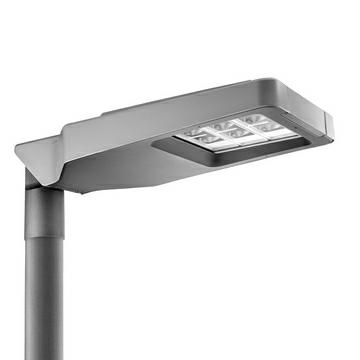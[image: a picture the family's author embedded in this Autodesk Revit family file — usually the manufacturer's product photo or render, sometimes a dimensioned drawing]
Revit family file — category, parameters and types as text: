
# Revit family: Lighting-StreetLighting-GEWISS-ROAD[5]MEDIUM-LED_OPTIC_WIDE_CLII
name_source: partatom
category: Apparecchi per illuminazione
units: mm (PartAtom-declared; Revit-internal decimal feet)

## family parameters
Basato su piano di lavoro = No
Condiviso = No
Punto di calcolo locali = No
Quota connettore circolare = Usa diametro
Sempre verticale = Sì
Sorgente d'illuminazione = No
Taglio con vuoti quando caricato = No
Tipo di parte = Normale

## types (73) — shared parameters
Applicazione = External
Catalogue = LIGHTING
IDF = 569e3ec7-4e66-4966-a072-a472dfe29722
IDT = e2497ca35bdb4cc4a5a8992b37b2b612
IP degree = IP66
Immagine tipo = GWR5276M.jpg
Insulation class = II
Lampada = LED
Produttore = GEWISS S.p.A.
Shock resistance = IK08
Technical sheet = https://www.gewiss.com
URL = https://www.gewiss.com
Version file RFA = 20.11
Warranty = 5 years

## per-type parameters (varying)
- GWR5253M - ROAD5 MEDI WIDE 3M 4000K 0,5A CL2 1-10V: Body=Die-cast aluminium -; Catalogue Range=ROAD [5]; Classification:=-; Color Rendering Index=CRI-70; Colore=Graphite grey; Colour :=Powder coating; Colour temperature=4000K; Colour temperature:=4000 K (CRI>70); Context=Street and parking lighting; Control System=Dimmable 1-10 V; DIN 18032-3 certification=-; Descrizione=GWR5253M - ROAD5 MEDI WIDE 3M 4000K 0,5A CL2 1-10V; Device with reduced surface temperature=-; Driver=Included; Driver Box=Built-in; Efficiency (lm/W)=121; Electrocod=244C; Eletrical and lighting features=-; External screw=Stainless steel; Fixing=Pole Head - Outreach; Gasket=Anti-aging silicone; General information=-; Glow Wire Test :=-; IPEA=ROAD = A5 + // LARGE AREAS = A6 + // CYCLOPEDONALS = A5 + // GREEN AREAS = A5 + // HISTORICAL CENTER = A6 +; Installationa and maintenance=-; LED Life Time (L80B05)=120000H; LED Maintenance=Not available; LED current.=0,5A; Lamp-=LED; Lifetime=L90B10 (Tq+25°C) = 100.000 h - L90B10 (Tq+50°C) = 75.000 h; Locking Hook=Integrated front handle; Lumen output (lm)=7000; Luminaire=LED Road Equipment; Materials=-; Maximum surface exposed to the wind=0,19M2; Maximum surface exposed to the wind :=0.19 m2; Minimum distance from the illuminated object=1M; Modello=GWR5253M; Mouting and installation=Pole Head - Outreach; Nominal flux (lm)=7200; Number of modules=3 (3x3 LED); Operating temperature :=-25 +50 °C; Operating temperature:=-25 +40 °C; Optic=WIDE; Optic :=Metallized polycarbonate reflector; Optic Maintenance=Not available; Optic and illuminating features=-; Overvoltage protection=DM 10KV / CM 10KV; Photobiological Risk Class=RG0; Rated frequency (Hz)=50 / 60; SEO=Street lighting; Shield type=4mm thick flat tempered glass; Standard Deviation Colour Matching=SDCM = 5; Standard-=EN 60598-2-3, EN 60598-1 IEC/TR 62778; Standards and approvals=-; Stocking temperature=-; Supply voltage=220 - 240 V; System power=54W; System power :=58 W @ 0.5A; Tilt adjustable=-20° ÷ +10° side bracket - -10° ÷ +20° pole head; Tilt-=-20° ÷ +10° side bracket - -10° ÷ +20° pole head; Tipologia=Dimmable; Type of light source=LED - Not replaceable; Unified Glare Rating=G*3 - ULOR = 0; Unique digital code (Datamatrix)=Currently not present; Voltage-=220/240 V - 50/60 Hz - Dimmable 1-10 V; Weight (kg):=8; Wiring=Isolating switch
- GWR5213M30K - ROAD5 MEDI WIDE 3M 3000K 1,0A CL2 1-10V: Body=Die-cast aluminium -; Catalogue Range=ROAD [5]; Classification:=-; Color Rendering Index=CRI-70; Colore=Graphite grey; Colour :=Powder coating; Colour temperature=3000K; Colour temperature:=3000 K (CRI>80); Context=Street and parking lighting; Control System=Dimmable 1-10 V; DIN 18032-3 certification=-; Descrizione=GWR5213M30K - ROAD5 MEDI WIDE 3M 3000K 1,0A CL2 1-10V; Device with reduced surface temperature=-; Driver=Included; Driver Box=Built-in; Efficiency (lm/W)=97; Electrocod=244C; Eletrical and lighting features=-; External screw=Stainless steel; Fixing=Pole Head - Outreach; Gasket=Anti-aging silicone; General information=-; Glow Wire Test :=-; IPEA=ROAD = A // LARGE AREAS = A ++ // CYCLOPEDONALS = A // GREEN AREAS = A // HISTORICAL CENTER = A3 +; Installationa and maintenance=-; LED Life Time (L80B05)=120000H; LED Maintenance=Not available; LED current.=1A; Lamp-=LED; Lifetime=L90B10 (Tq+25°C) = 100.000 h - L90B10 (Tq+40°C) = 75.000 h; Locking Hook=Integrated front handle; Lumen output (lm)=11100; Luminaire=LED Road Equipment; Materials=-; Maximum surface exposed to the wind=0,19M2; Maximum surface exposed to the wind :=0.19 m2; Minimum distance from the illuminated object=1M; Modello=GWR5213M30K; Mouting and installation=Pole Head - Outreach; Nominal flux (lm)=12420; Number of modules=3 (3x3 LED); Operating temperature :=-25 +40 °C; Operating temperature:=-25 +40 °C; Optic=WIDE; Optic :=Metallized polycarbonate reflector; Optic Maintenance=Not available; Optic and illuminating features=-; Overvoltage protection=DM 10KV / CM 10KV; Overvoltage resistance :=Common and dfferential mode: 10KV; Photobiological Risk Class=RG0; Power supply operation=Dimmable; Rated frequency (Hz)=50 / 60; SEO=Street lighting; Shield type=4mm thick flat tempered glass; Standard Deviation Colour Matching=SDCM = 5; Standard-=EN 60598-2-3, EN 60598-1 IEC/TR 62778; Standards and approvals=-; Stocking temperature=-; Supply voltage=220 - 240 V; System power=113W; System power :=115 W @ 1A; Tilt adjustable=-20° ÷ +10° side bracket - -10° ÷ +20° pole head; Tilt-=-20° ÷ +10° side bracket - -10° ÷ +20° pole head; Tipo alimentatore=Constant Current Driver Led; Tipologia=Dimmable; Type of light source=LED - Not replaceable; Unified Glare Rating=G*3 - ULOR = 0; Unique digital code (Datamatrix)=Currently not present; Voltage-=220/240 V - 50/60 Hz - Dimmable 1-10 V; Weight (kg):=8; Wiring=Isolating switch
- GWR521630K - ROAD5 MEDI WIDE 6M 3000K 0,85A CL2: Body=Die-cast aluminium -; Catalogue Range=ROAD [5]; Classification:=-; Color Rendering Index=CRI-70; Colore=Graphite grey; Colour :=Powder coating; Colour temperature=3000K; Colour temperature:=3000 K (CRI>80); Context=Street and parking lighting; Control System=Stand alone; DIN 18032-3 certification=-; Descrizione=GWR521630K - ROAD5 MEDI WIDE 6M 3000K 0,85A CL2; Device with reduced surface temperature=-; Driver=Included; Driver Box=Built-in; Efficiency (lm/W)=105; Electrocod=244C; Eletrical and lighting features=-; External screw=Stainless steel; Fixing=Pole Head - Outreach; Gasket=Anti-aging silicone; General information=-; Glow Wire Test :=-; IPEA=ROAD = B // LARGE AREAS = A ++ // CYCLOPEDONALS = A // GREEN AREAS = A // HISTORICAL CENTER = A3 +; Installationa and maintenance=-; LED Life Time (L80B05)=120000H; LED Maintenance=Not available; LED current.=0,849999999999999A; Lamp-=LED; Lifetime=L90B10 (Tq+25°C) = 100.000 h - L90B10 (Tq+40°C) = 50.000 h; Locking Hook=Integrated front handle; Lumen output (lm)=19400; Luminaire=LED Road Equipment; Materials=-; Maximum surface exposed to the wind=0,19M2; Maximum surface exposed to the wind :=0.19 m2; Minimum distance from the illuminated object=1M; Modello=GWR521630K; Mouting and installation=Pole Head - Outreach; Nominal flux (lm)=21114; Number of modules=6 (6x3 LED); Operating temperature :=-25 +40 °C; Operating temperature:=-25 +40 °C; Optic=WIDE; Optic :=Metallized polycarbonate reflector; Optic Maintenance=Not available; Optic and illuminating features=-; Overvoltage protection=DM 10KV / CM 10KV; Overvoltage resistance :=Common and dfferential mode: 10KV; Photobiological Risk Class=RG0; Rated frequency (Hz)=50 / 60; SEO=Street lighting; Shield type=4mm thick flat tempered glass; Standard Deviation Colour Matching=SDCM = 5; Standard-=EN 60598-2-3, EN 60598-1 IEC/TR 62778; Standards and approvals=-; Stocking temperature=-; Supply voltage=220 - 240 V; System power=185W; System power :=185 W @ 0.85A; Tilt adjustable=-20° ÷ +10° side bracket - -10° ÷ +20° pole head; Tilt-=-20° ÷ +10° side bracket - -10° ÷ +20° pole head; Tipo alimentatore=Constant Current Driver Led; Tipologia=Stand alone; Type of light source=LED - Not replaceable; Unified Glare Rating=G*3 - ULOR = 0; Unique digital code (Datamatrix)=Currently not present; Voltage-=220/240 V - 50/60 Hz - Stand alone; Weight (kg):=9,09999999999999; Wiring=Isolating switch
- GWR5254B - ROAD5 MEDI WIDE 4M 4000K 0,5A CL2 BIREG: Body=Die-cast aluminium -; Catalogue Range=ROAD [5]; Classification:=-; Color Rendering Index=CRI-70; Colore=Graphite grey; Colour :=Powder coating; Colour temperature=4000K; Colour temperature:=4000 K (CRI>70); Context=Street and parking lighting; Control System=Bi-power with self-learning; DIN 18032-3 certification=-; Descrizione=GWR5254B - ROAD5 MEDI WIDE 4M 4000K 0,5A CL2 BIREG; Device with reduced surface temperature=-; Driver=Included; Driver Box=Built-in; Efficiency (lm/W)=124; Electrocod=244C; Eletrical and lighting features=-; External screw=Stainless steel; Fixing=Pole Head - Outreach; Gasket=Anti-aging silicone; General information=-; Glow Wire Test :=-; IPEA=ROAD = A5 + // LARGE AREAS = A6 + // CYCLOPEDONALS = A4 + // GREEN AREAS = A4 + // HISTORICAL CENTER = A6 +; Installationa and maintenance=-; LED Life Time (L80B05)=120000H; LED Maintenance=Not available; LED current.=0,5A; Lamp-=LED; Lifetime=L90B10 (Tq+25°C) = 100.000 h - L90B10 (Tq+50°C) = 50.000 h; Locking Hook=Integrated front handle; Lumen output (lm)=9400; Luminaire=LED Road Equipment; Materials=-; Maximum surface exposed to the wind=0,19M2; Maximum surface exposed to the wind :=0.19 m2; Minimum distance from the illuminated object=1M; Modello=GWR5254B; Mouting and installation=Pole Head - Outreach; Nominal flux (lm)=9600; Number of modules=4 (4x3 LED); Operating temperature :=-25 +50 °C; Operating temperature:=-25 +40 °C; Optic=WIDE; Optic :=Metallized polycarbonate reflector; Optic Maintenance=Not available; Optic and illuminating features=-; Overvoltage protection=DM 10KV / CM 10KV; Photobiological Risk Class=RG0; Power supply operation=Bi power; Rated frequency (Hz)=50 / 60; SEO=Street lighting; Shield type=4mm thick flat tempered glass; Standard Deviation Colour Matching=SDCM = 5; Standard-=EN 60598-2-3, EN 60598-1 IEC/TR 62778; Standards and approvals=-; Stocking temperature=-; Supply voltage=220 - 240 V; System power=73W; System power :=76 W @ 0.5A; Tilt adjustable=-20° ÷ +10° side bracket - -10° ÷ +20° pole head; Tilt-=-20° ÷ +10° side bracket - -10° ÷ +20° pole head; Type of light source=LED - Not replaceable; Unified Glare Rating=G*3 - ULOR = 0; Unique digital code (Datamatrix)=Currently not present; Voltage-=220/240 V - 50/60 Hz - Bi-power with self-learning; Weight (kg):=8,4; Wiring=Isolating switch
- GWR5216M30K - ROAD5 MEDI WIDE 6M 3000K 0,85A CL2 1-10V: Body=Die-cast aluminium -; Catalogue Range=ROAD [5]; Classification:=-; Color Rendering Index=CRI-70; Colore=Graphite grey; Colour :=Powder coating; Colour temperature=3000K; Colour temperature:=3000 K (CRI>80); Context=Street and parking lighting; Control System=Dimmable 1-10 V; DIN 18032-3 certification=-; Descrizione=GWR5216M30K - ROAD5 MEDI WIDE 6M 3000K 0,85A CL2 1-10V; Device with reduced surface temperature=-; Driver=Included; Driver Box=Built-in; Efficiency (lm/W)=104; Electrocod=244C; Eletrical and lighting features=-; External screw=Stainless steel; Fixing=Pole Head - Outreach; Gasket=Anti-aging silicone; General information=-; Glow Wire Test :=-; IPEA=ROAD = B // LARGE AREAS = A ++ // CYCLOPEDONALS = A // GREEN AREAS = A // HISTORICAL CENTER = A3 +; Installationa and maintenance=-; LED Life Time (L80B05)=120000H; LED Maintenance=Not available; LED current.=0,849999999999999A; Lamp-=LED; Lifetime=L90B10 (Tq+25°C) = 100.000 h - L90B10 (Tq+40°C) = 50.000 h; Locking Hook=Integrated front handle; Lumen output (lm)=19400; Luminaire=LED Road Equipment; Materials=-; Maximum surface exposed to the wind=0,19M2; Maximum surface exposed to the wind :=0.19 m2; Minimum distance from the illuminated object=1M; Modello=GWR5216M30K; Mouting and installation=Pole Head - Outreach; Nominal flux (lm)=21114; Number of modules=6 (6x3 LED); Operating temperature :=-25 +40 °C; Operating temperature:=-25 +40 °C; Optic=WIDE; Optic :=Metallized polycarbonate reflector; Optic Maintenance=Not available; Optic and illuminating features=-; Overvoltage protection=DM 10KV / CM 10KV; Overvoltage resistance :=Common and dfferential mode: 10KV; Photobiological Risk Class=RG0; Power supply operation=Dimmable; Rated frequency (Hz)=50 / 60; SEO=Street lighting; Shield type=4mm thick flat tempered glass; Standard Deviation Colour Matching=SDCM = 5; Standard-=EN 60598-2-3, EN 60598-1 IEC/TR 62778; Standards and approvals=-; Stocking temperature=-; Supply voltage=220 - 240 V; System power=185W; System power :=187 W @ 0.85A; Tilt adjustable=-20° ÷ +10° side bracket - -10° ÷ +20° pole head; Tilt-=-20° ÷ +10° side bracket - -10° ÷ +20° pole head; Tipo alimentatore=Constant Current Driver Led; Tipologia=Dimmable; Type of light source=LED - Not replaceable; Unified Glare Rating=G*3 - ULOR = 0; Unique digital code (Datamatrix)=Currently not present; Voltage-=220/240 V - 50/60 Hz - Dimmable 1-10 V; Weight (kg):=9,09999999999999; Wiring=Isolating switch
- GWR5256D30K - ROAD5 MEDI WIDE 6M 3000K 0,5A CL2: Body=Die-cast aluminium -; Classification:=-; Color Rendering Index=CRI-70; Colore=Graphite grey; Colour :=Powder coating; Colour temperature=3000K; Context=Street and parking lighting; Control System=DALI; DIN 18032-3 certification=-; Descrizione=GWR5256D30K - ROAD5 MEDI WIDE 6M 3000K 0,5A CL2; Device with reduced surface temperature=-; Driver=Included; Driver Box=Built-in; Efficiency (lm/W)=108; Eletrical and lighting features=-; External screw=Stainless steel; Fixing=Pole Head - Outreach; Gasket=Anti-aging silicone; General information=-; Glow Wire Test :=-; IPEA=ROAD = A ++ // LARGE AREAS = A4 + // CYCLOPEDONALS = A + // GREEN AREAS = A + // HISTORICAL CENTER = A5 +; Installationa and maintenance=-; LED Maintenance=Not available; Lifetime=L90B10 (Tq+25°C) = 100.000 h - L90B10 (Tq+50°C) = 50.000 h; Locking Hook=Integrated front handle; Lumen output (lm)=12200; Luminaire=LED Road Equipment; Materials=-; Maximum surface exposed to the wind :=0.19 m2; Modello=GWR5256D30K; Mouting and installation=Pole Head - Outreach; Number of modules=6 (6x3 LED); Operating temperature :=-25 +50 °C; Optic=WIDE; Optic :=Metallized polycarbonate reflector; Optic Maintenance=Not available; Optic and illuminating features=-; Overvoltage protection=DM 10KV / CM 10KV; Photobiological Risk Class=RG0; Rated frequency (Hz)=50 / 60; SEO=Street lighting; Shield type=4mm thick flat tempered glass; Standard Deviation Colour Matching=SDCM = 5; Standard-=EN 60598-2-3, EN 60598-1 IEC/TR 62778; Standards and approvals=-; Stocking temperature=-; Supply voltage=220 - 240 V; System power :=113 W @ 0.5A; Tilt-=-20° ÷ +10° side bracket - -10° ÷ +20° pole head; Type of light source=LED - Not replaceable; Unified Glare Rating=G*3 - ULOR = 0; Unique digital code (Datamatrix)=Currently not present; Weight (kg):=9,09999999999999; Wiring=Isolating switch
- GWR5253B - ROAD5 MEDI WIDE 3M 4000K 0,5A CL2 BIREG: Body=Die-cast aluminium -; Catalogue Range=ROAD [5]; Classification:=-; Color Rendering Index=CRI-70; Colore=Graphite grey; Colour :=Powder coating; Colour temperature=4000K; Colour temperature:=4000 K (CRI>70); Context=Street and parking lighting; Control System=Bi-power with self-learning; DIN 18032-3 certification=-; Descrizione=GWR5253B - ROAD5 MEDI WIDE 3M 4000K 0,5A CL2 BIREG; Device with reduced surface temperature=-; Driver=Included; Driver Box=Built-in; Efficiency (lm/W)=121; Electrocod=244C; Eletrical and lighting features=-; External screw=Stainless steel; Fixing=Pole Head - Outreach; Gasket=Anti-aging silicone; General information=-; Glow Wire Test :=-; IPEA=ROAD = A5 + // LARGE AREAS = A6 + // CYCLOPEDONALS = A5 + // GREEN AREAS = A5 + // HISTORICAL CENTER = A6 +; Installationa and maintenance=-; LED Life Time (L80B05)=120000H; LED Maintenance=Not available; LED current.=0,5A; Lamp-=LED; Lifetime=L90B10 (Tq+25°C) = 100.000 h - L90B10 (Tq+50°C) = 75.000 h; Locking Hook=Integrated front handle; Lumen output (lm)=7000; Luminaire=LED Road Equipment; Materials=-; Maximum surface exposed to the wind=0,19M2; Maximum surface exposed to the wind :=0.19 m2; Minimum distance from the illuminated object=1M; Modello=GWR5253B; Mouting and installation=Pole Head - Outreach; Nominal flux (lm)=7200; Number of modules=3 (3x3 LED); Operating temperature :=-25 +50 °C; Operating temperature:=-25 +40 °C; Optic=WIDE; Optic :=Metallized polycarbonate reflector; Optic Maintenance=Not available; Optic and illuminating features=-; Overvoltage protection=DM 10KV / CM 10KV; Photobiological Risk Class=RG0; Power supply operation=Bi power; Rated frequency (Hz)=50 / 60; SEO=Street lighting; Shield type=4mm thick flat tempered glass; Standard Deviation Colour Matching=SDCM = 5; Standard-=EN 60598-2-3, EN 60598-1 IEC/TR 62778; Standards and approvals=-; Stocking temperature=-; Supply voltage=220 - 240 V; System power=54W; System power :=58 W @ 0.5A; Tilt adjustable=-20° ÷ +10° side bracket - -10° ÷ +20° pole head; Tilt-=-20° ÷ +10° side bracket - -10° ÷ +20° pole head; Type of light source=LED - Not replaceable; Unified Glare Rating=G*3 - ULOR = 0; Unique digital code (Datamatrix)=Currently not present; Voltage-=220/240 V - 50/60 Hz - Bi-power with self-learning; Weight (kg):=8; Wiring=Isolating switch
- GWR5215M30K - ROAD5 MEDI WIDE 5M 3000K 0,85A CL2 1-10V: Body=Die-cast aluminium -; Catalogue Range=ROAD [5]; Classification:=-; Color Rendering Index=CRI-70; Colore=Graphite grey; Colour :=Powder coating; Colour temperature=3000K; Colour temperature:=3000 K (CRI>80); Context=Street and parking lighting; Control System=Dimmable 1-10 V; DIN 18032-3 certification=-; Descrizione=GWR5215M30K - ROAD5 MEDI WIDE 5M 3000K 0,85A CL2 1-10V; Device with reduced surface temperature=-; Driver=Included; Driver Box=Built-in; Efficiency (lm/W)=101; Electrocod=244C; Eletrical and lighting features=-; External screw=Stainless steel; Fixing=Pole Head - Outreach; Gasket=Anti-aging silicone; General information=-; Glow Wire Test :=-; IPEA=ROAD = A // LARGE AREAS = A ++ // CYCLOPEDONALS = A // GREEN AREAS = A // HISTORICAL CENTER = A4 +; Installationa and maintenance=-; LED Life Time (L80B05)=120000H; LED Maintenance=Not available; LED current.=0,849999999999999A; Lamp-=LED; Lifetime=L90B10 (Tq+25°C) = 100.000 h - L90B10 (Tq+40°C) = 50.000 h; Locking Hook=Integrated front handle; Lumen output (lm)=16200; Luminaire=LED Road Equipment; Materials=-; Maximum surface exposed to the wind=0,19M2; Maximum surface exposed to the wind :=0.19 m2; Minimum distance from the illuminated object=1M; Modello=GWR5215M30K; Mouting and installation=Pole Head - Outreach; Nominal flux (lm)=18423; Number of modules=5 (5x3 LED); Operating temperature :=-25 +40 °C; Operating temperature:=-25 +40 °C; Optic=WIDE; Optic :=Metallized polycarbonate reflector; Optic Maintenance=Not available; Optic and illuminating features=-; Overvoltage protection=DM 10KV / CM 10KV; Overvoltage resistance :=Common and dfferential mode: 10KV; Photobiological Risk Class=RG0; Power supply operation=Dimmable; Rated frequency (Hz)=50 / 60; SEO=Street lighting; Shield type=4mm thick flat tempered glass; Standard Deviation Colour Matching=SDCM = 5; Standard-=EN 60598-2-3, EN 60598-1 IEC/TR 62778; Standards and approvals=-; Stocking temperature=-; Supply voltage=220 - 240 V; System power=159W; System power :=161 W @ 0.85A; Tilt adjustable=-20° ÷ +10° side bracket - -10° ÷ +20° pole head; Tilt-=-20° ÷ +10° side bracket - -10° ÷ +20° pole head; Tipo alimentatore=Constant Current Driver Led; Tipologia=Dimmable; Type of light source=LED - Not replaceable; Unified Glare Rating=G*3 - ULOR = 0; Unique digital code (Datamatrix)=Currently not present; Voltage-=220/240 V - 50/60 Hz - Dimmable 1-10 V; Weight (kg):=8,8; Wiring=Isolating switch
- GWR5274B - ROAD5 MEDI WIDE 4M 4000K 0,7A CL2 BIREG: Catalogue Range=ROAD [5]; Colour temperature=4000 K (CRI 70); Colour temperature:=4000 K (CRI 70); Descrizione=ROAD 5 MED.BIPOW.4M 4000K 700mA OPT.W; EAN code=8011564858466; Electrocod=244C; LED LifeTime (L80B05)=77000H; LED current.=0,7A; Lamp-=LED; Lumen output (lm)=10480; Maximum surface exposed to the wind=0,19M2; Minimum distance from the illuminated object=1M; Modello=GWR5274B; No. Chorus modules=4 (4x3 LED); Nominal flux (lm)=12480; Number of modules=4 (4x3 LED); Operating temperature:=-25 +50 °C; Optic=W - ULOR: 0%; Overvoltage resistance=12 KV (Common and dfferential mode); Pilot current=0,7A; Power supply operation=Bi power; SEO=Street lighting; System power=108W; Tilt adjustable=-20° ÷ +10° side bracket - -10° ÷ +20° pole head; Tipo alimentatore=Constant Current Driver Led; Tipologia=Bi power; Voltage-=220/240 V - 50/60 Hz - Bi-power with self-learning; Weight (kg):=8,4; Working temperature=-25 +50 °C
- GWR5213M - ROAD 5 MED.DIMM.3M 4000K 1A OPT.W: Catalogue Range=ROAD [5]; Colour temperature=4000 K (CRI 70); Colour temperature:=4000 K (CRI 70); Descrizione=ROAD 5 MED.DIMM.3M 4000K 1A OPT.W; EAN code=8011564858640; Electrocod=244C; LED LifeTime (L80B05)=120000H; LED current.=1A; Lamp-=LED; Lumen output (lm)=11520; Maximum surface exposed to the wind=0,19M2; Minimum distance from the illuminated object=1M; Modello=GWR5213M; No. Chorus modules=3 (3x3 LED); Nominal flux (lm)=14310; Number of modules=3 (3x3 LED); Operating temperature:=-25 +40 °C; Optic=W - ULOR: 0%; Overvoltage resistance=12 KV (Common and dfferential mode); Pilot current=1A; Power supply operation=Dimmable; SEO=Street lighting; System power=113W; Tilt adjustable=-20° ÷ +10° side bracket - -10° ÷ +20° pole head; Tipo alimentatore=Constant Current Driver Led; Tipologia=Dimmable; Voltage-=220/240 V - 50/60 Hz - Dimmable 1-10 V; Weight (kg)=8; Weight (kg):=8; Working temperature=-25 +40 °C
- GWR527430K - ROAD5 MEDI WIDE 4M 3000K 0,7A CL2: Body=Die-cast aluminium -; Catalogue Range=ROAD [5]; Classification:=-; Color Rendering Index=CRI-70; Colore=Graphite grey; Colour :=Powder coating; Colour temperature=3000K; Colour temperature:=3000 K (CRI>80); Context=Street and parking lighting; Control System=Stand alone; DIN 18032-3 certification=-; Descrizione=GWR527430K - ROAD5 MEDI WIDE 4M 3000K 0,7A CL2; Device with reduced surface temperature=-; Driver=Included; Driver Box=Built-in; Efficiency (lm/W)=104; Electrocod=244C; Eletrical and lighting features=-; External screw=Stainless steel; Fixing=Pole Head - Outreach; Gasket=Anti-aging silicone; General information=-; Glow Wire Test :=-; IPEA=ROAD = A + // LARGE AREAS = A3 + // CYCLOPEDONALS = A + // GREEN AREAS = A + // HISTORICAL CENTER = A4 +; Installationa and maintenance=-; LED Life Time (L80B05)=77000H; LED Maintenance=Not available; LED current.=0,7A; Lamp-=LED; Lifetime=L90B10 (Tq+25°C) = 100.000 h - L90B10 (Tq+50°C) = 50.000 h; Locking Hook=Integrated front handle; Lumen output (lm)=11000; Luminaire=LED Road Equipment; Materials=-; Maximum surface exposed to the wind=0,19M2; Maximum surface exposed to the wind :=0.19 m2; Minimum distance from the illuminated object=1M; Modello=GWR527430K; Mouting and installation=Pole Head - Outreach; Nominal flux (lm)=10800; Number of modules=4 (4x3 LED); Operating temperature :=-25 +50 °C; Operating temperature:=-25 +50 °C; Optic=WIDE; Optic :=Metallized polycarbonate reflector; Optic Maintenance=Not available; Optic and illuminating features=-; Overvoltage protection=DM 10KV / CM 10KV; Overvoltage resistance :=Common and dfferential mode: 10KV; Photobiological Risk Class=RG0; Rated frequency (Hz)=50 / 60; SEO=Street lighting; Shield type=4mm thick flat tempered glass; Standard Deviation Colour Matching=SDCM = 5; Standard-=EN 60598-2-3, EN 60598-1 IEC/TR 62778; Standards and approvals=-; Stocking temperature=-; Supply voltage=220 - 240 V; System power=106W; System power :=106 W @ 0.7A; Tilt adjustable=-20° ÷ +10° side bracket - -10° ÷ +20° pole head; Tilt-=-20° ÷ +10° side bracket - -10° ÷ +20° pole head; Tipo alimentatore=Constant Current Driver Led; Tipologia=Stand alone; Type of light source=LED - Not replaceable; Unified Glare Rating=G*3 - ULOR = 0; Unique digital code (Datamatrix)=Currently not present; Voltage-=220/240 V - 50/60 Hz - Stand alone; Weight (kg):=8,4; Wiring=Isolating switch
- GWR5275B - ROAD5 MEDI WIDE 5M 4000K 0,7A CL2 BIREG: Catalogue Range=ROAD [5]; Colour temperature=4000 K (CRI 70); Colour temperature:=4000 K (CRI 70); Descrizione=ROAD 5 MED.BIPOW.5M 4000K 700mA OPT.W; EAN code=8011564858497; Electrocod=244C; LED LifeTime (L80B05)=77000H; LED current.=0,7A; Lamp-=LED; Lumen output (lm)=13100; Maximum surface exposed to the wind=0,19M2; Minimum distance from the illuminated object=1M; Modello=GWR5275B; No. Chorus modules=5 (5x3 LED); Nominal flux (lm)=15600; Number of modules=5 (5x3 LED); Operating temperature:=-25 +50 °C; Optic=W - ULOR: 0%; Overvoltage resistance=12 KV (Common and dfferential mode); Pilot current=0,7A; Power supply operation=Bi power; SEO=Street lighting; System power=134W; Tilt adjustable=-20° ÷ +10° side bracket - -10° ÷ +20° pole head; Tipo alimentatore=Constant Current Driver Led; Tipologia=Bi power; Voltage-=220/240 V - 50/60 Hz - Bi-power with self-learning; Weight (kg)=8,8; Weight (kg):=8,8; Working temperature=-25 +50 °C
- GWR5275 - ROAD 5 MED.ST.AL.5M 4000K 700mA OPT.W: Catalogue Range=ROAD [5]; Colour temperature=4000 K (CRI 70); Colour temperature:=4000 K (CRI 70); Descrizione=ROAD 5 MED.ST.AL.5M 4000K 700mA OPT.W; EAN code=8011564858305; Electrocod=244C; LED LifeTime (L80B05)=77000H; LED current.=0,7A; Lamp-=LED; Lumen output (lm)=13100; Maximum surface exposed to the wind=0,19M2; Minimum distance from the illuminated object=1M; Modello=GWR5275; No. Chorus modules=5 (5x3 LED); Nominal flux (lm)=15600; Number of modules=5 (5x3 LED); Operating temperature:=-25 +50 °C; Optic=W - ULOR: 0%; Overvoltage resistance=12 KV (Common and dfferential mode); Pilot current=0,7A; SEO=Street lighting; System power=132W; Tilt adjustable=-20° ÷ +10° side bracket - -10° ÷ +20° pole head; Tipo alimentatore=Constant Current Driver Led; Tipologia=Stand alone; Voltage-=220/240 V - 50/60 Hz - Stand alone; Weight (kg)=8,8; Weight (kg):=8,8; Working temperature=-25 +50 °C
- GWR5276M30K - ROAD5 MEDI WIDE 6M 3000K 0,7A CL2 1-10V: Body=Die-cast aluminium -; Catalogue Range=ROAD [5]; Classification:=-; Color Rendering Index=CRI-70; Colore=Graphite grey; Colour :=Powder coating; Colour temperature=3000K; Colour temperature:=3000 K (CRI>80); Context=Street and parking lighting; Control System=Dimmable 1-10 V; DIN 18032-3 certification=-; Descrizione=GWR5276M30K - ROAD5 MEDI WIDE 6M 3000K 0,7A CL2 1-10V; Device with reduced surface temperature=-; Driver=Included; Driver Box=Built-in; Efficiency (lm/W)=102; Electrocod=244C; Eletrical and lighting features=-; External screw=Stainless steel; Fixing=Pole Head - Outreach; Gasket=Anti-aging silicone; General information=-; Glow Wire Test :=-; IPEA=ROAD = A // LARGE AREAS = A3 + // CYCLOPEDONALS = A // GREEN AREAS = A // HISTORICAL CENTER = A4 +; Installationa and maintenance=-; LED Life Time (L80B05)=77000H; LED Maintenance=Not available; LED current.=0,7A; Lamp-=LED; Lifetime=L90B10 (Tq+25°C) = 100.000 h - L90B10 (Tq+50°C) = 50.000 h; Locking Hook=Integrated front handle; Lumen output (lm)=16500; Luminaire=LED Road Equipment; Materials=-; Maximum surface exposed to the wind=0,19M2; Maximum surface exposed to the wind :=0.19 m2; Minimum distance from the illuminated object=1M; Modello=GWR5276M30K; Mouting and installation=Pole Head - Outreach; Nominal flux (lm)=16200; Number of modules=6 (6x3 LED); Operating temperature :=-25 +50 °C; Operating temperature:=-25 +50 °C; Optic=WIDE; Optic :=Metallized polycarbonate reflector; Optic Maintenance=Not available; Optic and illuminating features=-; Overvoltage protection=DM 10KV / CM 10KV; Overvoltage resistance :=Common and dfferential mode: 10KV; Photobiological Risk Class=RG0; Power supply operation=Dimmable; Rated frequency (Hz)=50 / 60; SEO=Street lighting; Shield type=4mm thick flat tempered glass; Standard Deviation Colour Matching=SDCM = 5; Standard-=EN 60598-2-3, EN 60598-1 IEC/TR 62778; Standards and approvals=-; Stocking temperature=-; Supply voltage=220 - 240 V; System power=159W; System power :=161 W @ 0.7A; Tilt adjustable=-20° ÷ +10° side bracket - -10° ÷ +20° pole head; Tilt-=-20° ÷ +10° side bracket - -10° ÷ +20° pole head; Tipo alimentatore=Constant Current Driver Led; Tipologia=Dimmable; Type of light source=LED - Not replaceable; Unified Glare Rating=G*3 - ULOR = 0; Unique digital code (Datamatrix)=Currently not present; Voltage-=220/240 V - 50/60 Hz - Dimmable 1-10 V; Weight (kg):=9,09999999999999; Wiring=Isolating switch
- GWR5274B30K - ROAD5 MEDI WIDE 4M 3000K 0,7A CL2 BIREG: Body=Die-cast aluminium -; Catalogue Range=ROAD [5]; Classification:=-; Color Rendering Index=CRI-70; Colore=Graphite grey; Colour :=Powder coating; Colour temperature=3000K; Colour temperature:=3000 K (CRI>80); Context=Street and parking lighting; Control System=Bi-power with self-learning; DIN 18032-3 certification=-; Descrizione=GWR5274B30K - ROAD5 MEDI WIDE 4M 3000K 0,7A CL2 BIREG; Device with reduced surface temperature=-; Driver=Included; Driver Box=Built-in; Efficiency (lm/W)=102; Electrocod=244C; Eletrical and lighting features=-; External screw=Stainless steel; Fixing=Pole Head - Outreach; Gasket=Anti-aging silicone; General information=-; Glow Wire Test :=-; IPEA=ROAD = A + // LARGE AREAS = A3 + // CYCLOPEDONALS = A // GREEN AREAS = A // HISTORICAL CENTER = A4 +; Installationa and maintenance=-; LED Life Time (L80B05)=77000H; LED Maintenance=Not available; LED current.=0,7A; Lamp-=LED; Lifetime=L90B10 (Tq+25°C) = 100.000 h - L90B10 (Tq+50°C) = 50.000 h; Locking Hook=Integrated front handle; Lumen output (lm)=11000; Luminaire=LED Road Equipment; Materials=-; Maximum surface exposed to the wind=0,19M2; Maximum surface exposed to the wind :=0.19 m2; Minimum distance from the illuminated object=1M; Modello=GWR5274B30K; Mouting and installation=Pole Head - Outreach; Nominal flux (lm)=10800; Number of modules=4 (4x3 LED); Operating temperature :=-25 +50 °C; Operating temperature:=-25 +50 °C; Optic=WIDE; Optic :=Metallized polycarbonate reflector; Optic Maintenance=Not available; Optic and illuminating features=-; Overvoltage protection=DM 10KV / CM 10KV; Overvoltage resistance :=Common and dfferential mode: 10KV; Photobiological Risk Class=RG0; Power supply operation=Bi power; Rated frequency (Hz)=50 / 60; SEO=Street lighting; Shield type=4mm thick flat tempered glass; Standard Deviation Colour Matching=SDCM = 5; Standard-=EN 60598-2-3, EN 60598-1 IEC/TR 62778; Standards and approvals=-; Stocking temperature=-; Supply voltage=220 - 240 V; System power=108W; System power :=108 W @ 0.7A; Tilt adjustable=-20° ÷ +10° side bracket - -10° ÷ +20° pole head; Tilt-=-20° ÷ +10° side bracket - -10° ÷ +20° pole head; Tipo alimentatore=Constant Current Driver Led; Tipologia=Bi power; Type of light source=LED - Not replaceable; Unified Glare Rating=G*3 - ULOR = 0; Unique digital code (Datamatrix)=Currently not present; Voltage-=220/240 V - 50/60 Hz - Bi-power with self-learning; Weight (kg):=8,4; Wiring=Isolating switch
- GWR5216 - ROAD 5 MED.ST.AL.6M 4000K 0,85A OPT.W: Catalogue Range=ROAD [5]; Colour temperature=4000 K (CRI 70); Colour temperature:=4000 K (CRI 70); Descrizione=ROAD 5 MED.ST.AL.6M 4000K 0,85A OPT.W; EAN code=8011564858435; Electrocod=244C; LED LifeTime (L80B05)=120000H; LED current.=0,85A; Lamp-=LED; Lumen output (lm)=19580; Maximum surface exposed to the wind=0,19M2; Minimum distance from the illuminated object=1M; Modello=GWR5216; No. Chorus modules=6 (6x3 LED); Nominal flux (lm)=24330; Number of modules=6 (6x3 LED); Operating temperature:=-25 +40 °C; Optic=W - ULOR: 0%; Overvoltage resistance=12 KV (Common and dfferential mode); Pilot current=0,85A; SEO=Street lighting; System power=185W; Tilt adjustable=-20° ÷ +10° side bracket - -10° ÷ +20° pole head; Tipo alimentatore=Constant Current Driver Led; Tipologia=Stand alone; Voltage-=220/240 V - 50/60 Hz - Stand alone; Weight (kg)=9.1; Weight (kg):=9,1; Working temperature=-25 +40 °C
- GWR5275V - ROAD5 MEDI V.WIDE 5M 4000K 0,7A CL2: Body=Die-cast aluminium -; Catalogue Range=ROAD [5]; Classification:=-; Color Rendering Index=CRI-70; Colore=Graphite grey; Colour :=Powder coating; Colour temperature=4000K; Colour temperature:=4000 K (CRI>70); Context=Street and parking lighting; Control System=DALI - 5 Step; DIN 18032-3 certification=-; Descrizione=GWR5275V - ROAD5 MEDI V.WIDE 5M 4000K 0,7A CL2; Device with reduced surface temperature=-; Driver=Included; Driver Box=Built-in; Efficiency (lm/W)=118; Electrocod=244C; Eletrical and lighting features=-; External screw=Stainless steel; Fixing=Pole Head - Outreach; Gasket=Anti-aging silicone; General information=-; Glow Wire Test :=-; IPEA=ROAD = A ++ // LARGE AREAS = A5 + // CYCLOPEDONALS = A ++ // GREEN AREAS = A ++ // HISTORICAL CENTER = A6 +; Installationa and maintenance=-; LED Life Time (L80B05)=120000H; LED Maintenance=Not available; LED current.=0,7A; Lamp-=LED; Lifetime=L90B10 (Tq+25°C) = 100.000 h - L90B10 (Tq+50°C) = 50.000 h; Locking Hook=Integrated front handle; Lumen output (lm)=15800; Luminaire=LED Road Equipment; Materials=-; Maximum surface exposed to the wind=0,19M2; Maximum surface exposed to the wind :=0.19 m2; Minimum distance from the illuminated object=1M; Modello=GWR5275V; Mouting and installation=Pole Head - Outreach; Nominal flux (lm)=15600; Number of modules=5 (5x3 LED); Operating temperature :=-25 +50 °C; Operating temperature:=-25 +40 °C; Optic=WIDE; Optic :=Metallized polycarbonate reflector; Optic Maintenance=Not available; Optic and illuminating features=-; Overvoltage protection=DM 10KV / CM 10KV; Photobiological Risk Class=RG0; Rated frequency (Hz)=50 / 60; SEO=Street lighting; Shield type=4mm thick flat tempered glass; Standard Deviation Colour Matching=SDCM = 5; Standard-=EN 60598-2-3, EN 60598-1 IEC/TR 62778; Standards and approvals=-; Stocking temperature=-; Supply voltage=220 - 240 V; System power=132W; System power :=134 W @ 0.7A; Tilt adjustable=-20° ÷ +10° side bracket - -10° ÷ +20° pole head; Tilt-=-20° ÷ +10° side bracket - -10° ÷ +20° pole head; Tipologia=Programmable (5 step); Type of light source=LED - Not replaceable; Unified Glare Rating=G*3 - ULOR = 0; Unique digital code (Datamatrix)=Currently not present; Voltage-=220/240 V - 50/60 Hz - Stand alone and/or programmable; Weight (kg):=8,8; Wiring=Isolating switch
- GWR5273V - ROAD5 MEDI V.WIDE 3M 4000K 0,7A CL2: Body=Die-cast aluminium -; Catalogue Range=ROAD [5]; Classification:=-; Color Rendering Index=CRI-70; Colore=Graphite grey; Colour :=Powder coating; Colour temperature=4000K; Colour temperature:=4000 K (CRI>70); Context=Street and parking lighting; Control System=DALI - 5 Step; DIN 18032-3 certification=-; Descrizione=GWR5273V - ROAD5 MEDI V.WIDE 3M 4000K 0,7A CL2; Device with reduced surface temperature=-; Driver=Included; Driver Box=Built-in; Efficiency (lm/W)=117; Electrocod=244C; Eletrical and lighting features=-; External screw=Stainless steel; Fixing=Pole Head - Outreach; Gasket=Anti-aging silicone; General information=-; Glow Wire Test :=-; IPEA=ROAD = A4 + // LARGE AREAS = A5 + // CYCLOPEDONALS = A3 + // GREEN AREAS = A3 + // HISTORICAL CENTER = A6 +; Installationa and maintenance=-; LED Life Time (L80B05)=120000H; LED Maintenance=Not available; LED current.=0,7A; Lamp-=LED; Lifetime=L90B10 (Tq+25°C) = 100.000 h - L90B10 (Tq+50°C) = 75.000 h; Locking Hook=Integrated front handle; Lumen output (lm)=9500; Luminaire=LED Road Equipment; Materials=-; Maximum surface exposed to the wind=0,19M2; Maximum surface exposed to the wind :=0.19 m2; Minimum distance from the illuminated object=1M; Modello=GWR5273V; Mouting and installation=Pole Head - Outreach; Nominal flux (lm)=9360; Number of modules=3 (3x3 LED); Operating temperature :=-25 +50 °C; Operating temperature:=-25 +40 °C; Optic=WIDE; Optic :=Metallized polycarbonate reflector; Optic Maintenance=Not available; Optic and illuminating features=-; Overvoltage protection=DM 10KV / CM 10KV; Photobiological Risk Class=RG0; Rated frequency (Hz)=50 / 60; SEO=Street lighting; Shield type=4mm thick flat tempered glass; Standard Deviation Colour Matching=SDCM = 5; Standard-=EN 60598-2-3, EN 60598-1 IEC/TR 62778; Standards and approvals=-; Stocking temperature=-; Supply voltage=220 - 240 V; System power=79W; System power :=81 W @ 0.7A; Tilt adjustable=-20° ÷ +10° side bracket - -10° ÷ +20° pole head; Tilt-=-20° ÷ +10° side bracket - -10° ÷ +20° pole head; Tipologia=Programmable (5 step); Type of light source=LED - Not replaceable; Unified Glare Rating=G*3 - ULOR = 0; Unique digital code (Datamatrix)=Currently not present; Voltage-=220/240 V - 50/60 Hz - Stand alone and/or programmable; Weight (kg):=8; Wiring=Isolating switch
- GWR5215B - ROAD5 MEDI WIDE 5M 4000K 0,85A CL2 BIREG: Catalogue Range=ROAD [5]; Colour temperature=4000 K (CRI 70); Colour temperature:=4000 K (CRI 70); Descrizione=ROAD 5 MED.BIPOW.5M 4000K 0,85A OPT.W; EAN code=8011564858503; Electrocod=244C; LED LifeTime (L80B05)=120000H; LED current.=0,85A; Lamp-=LED; Lumen output (lm)=17090; Maximum surface exposed to the wind=0,19M2; Minimum distance from the illuminated object=1M; Modello=GWR5215B; No. Chorus modules=5 (5x3 LED); Nominal flux (lm)=21230; Number of modules=5 (5x3 LED); Operating temperature:=-25 +40 °C; Optic=W - ULOR: 0%; Overvoltage resistance=12 KV (Common and dfferential mode); Pilot current=0,85A; Power supply operation=Bi power; SEO=Street lighting; System power=161W; Tilt adjustable=-20° ÷ +10° side bracket - -10° ÷ +20° pole head; Tipo alimentatore=Constant Current Driver Led; Tipologia=Bi power; Voltage-=220/240 V - 50/60 Hz - Bi-power with self-learning; Weight (kg)=8,8; Weight (kg):=8,8; Working temperature=-25 +40 °C
- GWR5214V - ROAD5 MEDI V.WIDE 4M 4000K 1,0A CL2: Body=Die-cast aluminium -; Catalogue Range=ROAD [5]; Classification:=-; Color Rendering Index=CRI-70; Colore=Graphite grey; Colour :=Powder coating; Colour temperature=4000K; Colour temperature:=4000 K (CRI>70); Context=Street and parking lighting; Control System=DALI - 5 Step; DIN 18032-3 certification=-; Descrizione=GWR5214V - ROAD5 MEDI V.WIDE 4M 4000K 1,0A CL2; Device with reduced surface temperature=-; Driver=Included; Driver Box=Built-in; Efficiency (lm/W)=111; Electrocod=244C; Eletrical and lighting features=-; External screw=Stainless steel; Fixing=Pole Head - Outreach; Gasket=Anti-aging silicone; General information=-; Glow Wire Test :=-; IPEA=ROAD = A + // LARGE AREAS = A4 + // CYCLOPEDONALS = A + // GREEN AREAS = A + // HISTORICAL CENTER = A6 +; Installationa and maintenance=-; LED Life Time (L80B05)=120000H; LED Maintenance=Not available; LED current.=1A; Lamp-=LED; Lifetime=L90B10 (Tq+25°C) = 100.000 h - L90B10 (Tq+40°C) = 50.000 h; Locking Hook=Integrated front handle; Lumen output (lm)=17000; Luminaire=LED Road Equipment; Materials=-; Maximum surface exposed to the wind=0,19M2; Maximum surface exposed to the wind :=0.19 m2; Minimum distance from the illuminated object=1M; Modello=GWR5214V; Mouting and installation=Pole Head - Outreach; Nominal flux (lm)=19080; Number of modules=4 (4x3 LED); Operating temperature :=-25 +40 °C; Operating temperature:=-25 +40 °C; Optic=WIDE; Optic :=Metallized polycarbonate reflector; Optic Maintenance=Not available; Optic and illuminating features=-; Overvoltage protection=DM 10KV / CM 10KV; Photobiological Risk Class=RG0; Rated frequency (Hz)=50 / 60; SEO=Street lighting; Shield type=4mm thick flat tempered glass; Standard Deviation Colour Matching=SDCM = 5; Standard-=EN 60598-2-3, EN 60598-1 IEC/TR 62778; Standards and approvals=-; Stocking temperature=-; Supply voltage=220 - 240 V; System power=151W; System power :=153 W @ 1A; Tilt adjustable=-20° ÷ +10° side bracket - -10° ÷ +20° pole head; Tilt-=-20° ÷ +10° side bracket - -10° ÷ +20° pole head; Tipologia=Programmable (5 step); Type of light source=LED - Not replaceable; Unified Glare Rating=G*3 - ULOR = 0; Unique digital code (Datamatrix)=Currently not present; Voltage-=220/240 V - 50/60 Hz - Stand alone and/or programmable; Weight (kg):=8,4; Wiring=Isolating switch
- GWR5274 - ROAD 5 MED.ST.AL.4M 4000K 700mA OPT.W: Catalogue Range=ROAD [5]; Colour temperature=4000 K (CRI 70); Colour temperature:=4000 K (CRI 70); Descrizione=ROAD 5 MED.ST.AL.4M 4000K 700mA OPT.W; EAN code=8011564858282; Electrocod=244C; LED LifeTime (L80B05)=77000H; LED current.=0,7A; Lamp-=LED; Lumen output (lm)=10480; Maximum surface exposed to the wind=0,19M2; Minimum distance from the illuminated object=1M; Modello=GWR5274; No. Chorus modules=4 (4x3 LED); Nominal flux (lm)=12480; Number of modules=4 (4x3 LED); Operating temperature:=-25 +50 °C; Optic=W - ULOR: 0%; Overvoltage resistance=12 KV (Common and dfferential mode); Pilot current=0,7A; SEO=Street lighting; System power=106W; Tilt adjustable=-20° ÷ +10° side bracket - -10° ÷ +20° pole head; Tipo alimentatore=Constant Current Driver Led; Tipologia=Stand alone; Voltage-=220/240 V - 50/60 Hz - Stand alone; Weight (kg)=8,4; Weight (kg):=8,4; Working temperature=-25 +50 °C
- GWR5215 - ROAD 5 MED.ST.AL.5M 4000K 0,85A OPT.W: Catalogue Range=ROAD [5]; Colour temperature=4000 K (CRI 70); Colour temperature:=4000 K (CRI 70); Descrizione=ROAD 5 MED.ST.AL.5M 4000K 0,85A OPT.W; EAN code=8011564858411; Electrocod=244C; LED LifeTime (L80B05)=120000H; LED current.=0,85A; Lamp-=LED; Lumen output (lm)=17090; Maximum surface exposed to the wind=0,19M2; Minimum distance from the illuminated object=1M; Modello=GWR5215; No. Chorus modules=5 (5x3 LED); Nominal flux (lm)=21230; Number of modules=5 (5x3 LED); Operating temperature:=-25 +40 °C; Optic=W - ULOR: 0%; Overvoltage resistance=12 KV (Common and dfferential mode); Pilot current=0,85A; SEO=Street lighting; System power=159W; Tilt adjustable=-20° ÷ +10° side bracket - -10° ÷ +20° pole head; Tipo alimentatore=Constant Current Driver Led; Tipologia=Stand alone; Voltage-=220/240 V - 50/60 Hz - Stand alone; Weight (kg)=8,8; Weight (kg):=8,8; Working temperature=-25 +40 °C
- GWR5276V - ROAD5 MEDI V.WIDE 6M 4000K 0,7A CL2: Body=Die-cast aluminium -; Catalogue Range=ROAD [5]; Classification:=-; Color Rendering Index=CRI-70; Colore=Graphite grey; Colour :=Powder coating; Colour temperature=4000K; Colour temperature:=4000 K (CRI>70); Context=Street and parking lighting; Control System=DALI - 5 Step; DIN 18032-3 certification=-; Descrizione=GWR5276V - ROAD5 MEDI V.WIDE 6M 4000K 0,7A CL2; Device with reduced surface temperature=-; Driver=Included; Driver Box=Built-in; Efficiency (lm/W)=118; Electrocod=244C; Eletrical and lighting features=-; External screw=Stainless steel; Fixing=Pole Head - Outreach; Gasket=Anti-aging silicone; General information=-; Glow Wire Test :=-; IPEA=ROAD = A ++ // LARGE AREAS = A5 + // CYCLOPEDONALS = A ++ // GREEN AREAS = A ++ // HISTORICAL CENTER = A6 +; Installationa and maintenance=-; LED Life Time (L80B05)=120000H; LED Maintenance=Not available; LED current.=0,7A; Lamp-=LED; Lifetime=L90B10 (Tq+25°C) = 100.000 h - L90B10 (Tq+50°C) = 50.000 h; Locking Hook=Integrated front handle; Lumen output (lm)=19000; Luminaire=LED Road Equipment; Materials=-; Maximum surface exposed to the wind=0,19M2; Maximum surface exposed to the wind :=0.19 m2; Minimum distance from the illuminated object=1M; Modello=GWR5276V; Mouting and installation=Pole Head - Outreach; Nominal flux (lm)=18720; Number of modules=6 (6x3 LED); Operating temperature :=-25 +50 °C; Operating temperature:=-25 +40 °C; Optic=WIDE; Optic :=Metallized polycarbonate reflector; Optic Maintenance=Not available; Optic and illuminating features=-; Overvoltage protection=DM 10KV / CM 10KV; Photobiological Risk Class=RG0; Rated frequency (Hz)=50 / 60; SEO=Street lighting; Shield type=4mm thick flat tempered glass; Standard Deviation Colour Matching=SDCM = 5; Standard-=EN 60598-2-3, EN 60598-1 IEC/TR 62778; Standards and approvals=-; Stocking temperature=-; Supply voltage=220 - 240 V; System power=159W; System power :=161 W @ 0.7A; Tilt adjustable=-20° ÷ +10° side bracket - -10° ÷ +20° pole head; Tilt-=-20° ÷ +10° side bracket - -10° ÷ +20° pole head; Tipologia=Programmable (5 step); Type of light source=LED - Not replaceable; Unified Glare Rating=G*3 - ULOR = 0; Unique digital code (Datamatrix)=Currently not present; Voltage-=220/240 V - 50/60 Hz - Stand alone and/or programmable; Weight (kg):=9,09999999999999; Wiring=Isolating switch
- GWR5276B - ROAD5 MEDI WIDE 6M 4000K 0,7A CL2 BIREG: Catalogue Range=ROAD [5]; Colour temperature=4000 K (CRI 70); Colour temperature:=4000 K (CRI 70); Descrizione=ROAD 5 MED.BIPOW.6M 4000K 700mA OPT.W; EAN code=8011564858619; Electrocod=244C; LED LifeTime (L80B05)=77000H; LED current.=0,7A; Lamp-=LED; Lumen output (lm)=15730; Maximum surface exposed to the wind=0,19M2; Minimum distance from the illuminated object=1M; Modello=GWR5276B; No. Chorus modules=6 (6x3 LED); Nominal flux (lm)=18720; Number of modules=6 (6x3 LED); Operating temperature:=-25 +50 °C; Optic=W - ULOR: 0%; Overvoltage resistance=12 KV (Common and dfferential mode); Pilot current=0,7A; Power supply operation=Bi power; SEO=Street lighting; System power=161W; Tilt adjustable=-20° ÷ +10° side bracket - -10° ÷ +20° pole head; Tipo alimentatore=Constant Current Driver Led; Tipologia=Bi power; Voltage-=220/240 V - 50/60 Hz - Bi-power with self-learning; Weight (kg)=9.1; Weight (kg):=9,1; Working temperature=-25 +50 °C
- GWR527330K - ROAD5 MEDI WIDE 3M 3000K 0,7A CL2: Body=Die-cast aluminium -; Catalogue Range=ROAD [5]; Classification:=-; Color Rendering Index=CRI-70; Colore=Graphite grey; Colour :=Powder coating; Colour temperature=3000K; Colour temperature:=3000 K (CRI>80); Context=Street and parking lighting; Control System=Stand alone; DIN 18032-3 certification=-; Descrizione=GWR527330K - ROAD5 MEDI WIDE 3M 3000K 0,7A CL2; Device with reduced surface temperature=-; Driver=Included; Driver Box=Built-in; Efficiency (lm/W)=105; Electrocod=244C; Eletrical and lighting features=-; External screw=Stainless steel; Fixing=Pole Head - Outreach; Gasket=Anti-aging silicone; General information=-; Glow Wire Test :=-; IPEA=ROAD = A3 + // LARGE AREAS = A4 + // CYCLOPEDONALS = A ++ // GREEN AREAS = A ++ // HISTORICAL CENTER = A6 +; Installationa and maintenance=-; LED Life Time (L80B05)=77000H; LED Maintenance=Not available; LED current.=0,7A; Lamp-=LED; Lifetime=L90B10 (Tq+25°C) = 100.000 h - L90B10 (Tq+50°C) = 75.000 h; Locking Hook=Integrated front handle; Lumen output (lm)=8300; Luminaire=LED Road Equipment; Materials=-; Maximum surface exposed to the wind=0,19M2; Maximum surface exposed to the wind :=0.19 m2; Minimum distance from the illuminated object=1M; Modello=GWR527330K; Mouting and installation=Pole Head - Outreach; Nominal flux (lm)=8100; Number of modules=3 (3x3 LED); Operating temperature :=-25 +50 °C; Operating temperature:=-25 +50 °C; Optic=WIDE; Optic :=Metallized polycarbonate reflector; Optic Maintenance=Not available; Optic and illuminating features=-; Overvoltage protection=DM 10KV / CM 10KV; Overvoltage resistance :=Common and dfferential mode: 10KV; Photobiological Risk Class=RG0; Rated frequency (Hz)=50 / 60; SEO=Street lighting; Shield type=4mm thick flat tempered glass; Standard Deviation Colour Matching=SDCM = 5; Standard-=EN 60598-2-3, EN 60598-1 IEC/TR 62778; Standards and approvals=-; Stocking temperature=-; Supply voltage=220 - 240 V; System power=79W; System power :=79 W @ 0.7A; Tilt adjustable=-20° ÷ +10° side bracket - -10° ÷ +20° pole head; Tilt-=-20° ÷ +10° side bracket - -10° ÷ +20° pole head; Tipo alimentatore=Constant Current Driver Led; Tipologia=Stand alone; Type of light source=LED - Not replaceable; Unified Glare Rating=G*3 - ULOR = 0; Unique digital code (Datamatrix)=Currently not present; Voltage-=220/240 V - 50/60 Hz - Stand alone; Weight (kg):=8; Wiring=Isolating switch
- GWR521530K - ROAD5 MEDI WIDE 5M 3000K 0,85A CL2: Body=Die-cast aluminium -; Catalogue Range=ROAD [5]; Classification:=-; Color Rendering Index=CRI-70; Colore=Graphite grey; Colour :=Powder coating; Colour temperature=3000K; Colour temperature:=3000 K (CRI>80); Context=Street and parking lighting; Control System=Stand alone; DIN 18032-3 certification=-; Descrizione=GWR521530K - ROAD5 MEDI WIDE 5M 3000K 0,85A CL2; Device with reduced surface temperature=-; Driver=Included; Driver Box=Built-in; Efficiency (lm/W)=102; Electrocod=244C; Eletrical and lighting features=-; External screw=Stainless steel; Fixing=Pole Head - Outreach; Gasket=Anti-aging silicone; General information=-; Glow Wire Test :=-; IPEA=ROAD = A // LARGE AREAS = A3 + // CYCLOPEDONALS = A // GREEN AREAS = A // HISTORICAL CENTER = A4 +; Installationa and maintenance=-; LED Life Time (L80B05)=120000H; LED Maintenance=Not available; LED current.=0,849999999999999A; Lamp-=LED; Lifetime=L90B10 (Tq+25°C) = 100.000 h - L90B10 (Tq+40°C) = 50.000 h; Locking Hook=Integrated front handle; Lumen output (lm)=16200; Luminaire=LED Road Equipment; Materials=-; Maximum surface exposed to the wind=0,19M2; Maximum surface exposed to the wind :=0.19 m2; Minimum distance from the illuminated object=1M; Modello=GWR521530K; Mouting and installation=Pole Head - Outreach; Nominal flux (lm)=18423; Number of modules=5 (5x3 LED); Operating temperature :=-25 +40 °C; Operating temperature:=-25 +40 °C; Optic=WIDE; Optic :=Metallized polycarbonate reflector; Optic Maintenance=Not available; Optic and illuminating features=-; Overvoltage protection=DM 10KV / CM 10KV; Overvoltage resistance :=Common and dfferential mode: 10KV; Photobiological Risk Class=RG0; Rated frequency (Hz)=50 / 60; SEO=Street lighting; Shield type=4mm thick flat tempered glass; Standard Deviation Colour Matching=SDCM = 5; Standard-=EN 60598-2-3, EN 60598-1 IEC/TR 62778; Standards and approvals=-; Stocking temperature=-; Supply voltage=220 - 240 V; System power=159W; System power :=159 W @ 0.85A; Tilt adjustable=-20° ÷ +10° side bracket - -10° ÷ +20° pole head; Tilt-=-20° ÷ +10° side bracket - -10° ÷ +20° pole head; Tipo alimentatore=Constant Current Driver Led; Tipologia=Stand alone; Type of light source=LED - Not replaceable; Unified Glare Rating=G*3 - ULOR = 0; Unique digital code (Datamatrix)=Currently not present; Voltage-=220/240 V - 50/60 Hz - Stand alone; Weight (kg):=8,8; Wiring=Isolating switch
- GWR5214M - ROAD5 MEDI WIDE 4M 4000K 1,0A CL2 1-10V: Catalogue Range=ROAD [5]; Colour temperature=4000 K (CRI 70); Colour temperature:=4000 K (CRI 70); Descrizione=ROAD 5 MED.DIMM.4M 4000K 1A OPT.W; EAN code=8011564858664; Electrocod=244C; LED LifeTime (L80B05)=120000H; LED current.=1A; Lamp-=LED; Lumen output (lm)=15360; Maximum surface exposed to the wind=0,19M2; Minimum distance from the illuminated object=1M; Modello=GWR5214M; No. Chorus modules=4 (4x3 LED); Nominal flux (lm)=19080; Number of modules=4 (4x3 LED); Operating temperature:=-25 +40 °C; Optic=W - ULOR: 0%; Overvoltage resistance=12 KV (Common and dfferential mode); Pilot current=1A; Power supply operation=Dimmable; SEO=Street lighting; System power=113W; Tilt adjustable=-20° ÷ +10° side bracket - -10° ÷ +20° pole head; Tipo alimentatore=Constant Current Driver Led; Tipologia=Dimmable; Voltage-=220/240 V - 50/60 Hz - Dimmable 1-10 V; Weight (kg)=8,4; Weight (kg):=8,4; Working temperature=-25 +40 °C
- GWR5275B30K - ROAD5 MEDI WIDE 5M 3000K 0,7A CL2 BIREG: Body=Die-cast aluminium -; Catalogue Range=ROAD [5]; Classification:=-; Color Rendering Index=CRI-70; Colore=Graphite grey; Colour :=Powder coating; Colour temperature=3000K; Colour temperature:=3000 K (CRI>80); Context=Street and parking lighting; Control System=Bi-power with self-learning; DIN 18032-3 certification=-; Descrizione=GWR5275B30K - ROAD5 MEDI WIDE 5M 3000K 0,7A CL2 BIREG; Device with reduced surface temperature=-; Driver=Included; Driver Box=Built-in; Efficiency (lm/W)=102; Electrocod=244C; Eletrical and lighting features=-; External screw=Stainless steel; Fixing=Pole Head - Outreach; Gasket=Anti-aging silicone; General information=-; Glow Wire Test :=-; IPEA=ROAD = A // LARGE AREAS = A3 + // CYCLOPEDONALS = A // GREEN AREAS = A // HISTORICAL CENTER = A4 +; Installationa and maintenance=-; LED Life Time (L80B05)=77000H; LED Maintenance=Not available; LED current.=0,7A; Lamp-=LED; Lifetime=L90B10 (Tq+25°C) = 100.000 h - L90B10 (Tq+50°C) = 50.000 h; Locking Hook=Integrated front handle; Lumen output (lm)=13700; Luminaire=LED Road Equipment; Materials=-; Maximum surface exposed to the wind=0,19M2; Maximum surface exposed to the wind :=0.19 m2; Minimum distance from the illuminated object=1M; Modello=GWR5275B30K; Mouting and installation=Pole Head - Outreach; Nominal flux (lm)=13500; Number of modules=5 (5x3 LED); Operating temperature :=-25 +50 °C; Operating temperature:=-25 +50 °C; Optic=WIDE; Optic :=Metallized polycarbonate reflector; Optic Maintenance=Not available; Optic and illuminating features=-; Overvoltage protection=DM 10KV / CM 10KV; Overvoltage resistance :=Common and dfferential mode: 10KV; Photobiological Risk Class=RG0; Power supply operation=Bi power; Rated frequency (Hz)=50 / 60; SEO=Street lighting; Shield type=4mm thick flat tempered glass; Standard Deviation Colour Matching=SDCM = 5; Standard-=EN 60598-2-3, EN 60598-1 IEC/TR 62778; Standards and approvals=-; Stocking temperature=-; Supply voltage=220 - 240 V; System power=134W; System power :=134 W @ 0.7A; Tilt adjustable=-20° ÷ +10° side bracket - -10° ÷ +20° pole head; Tilt-=-20° ÷ +10° side bracket - -10° ÷ +20° pole head; Tipo alimentatore=Constant Current Driver Led; Tipologia=Bi power; Type of light source=LED - Not replaceable; Unified Glare Rating=G*3 - ULOR = 0; Unique digital code (Datamatrix)=Currently not present; Voltage-=220/240 V - 50/60 Hz - Bi-power with self-learning; Weight (kg):=8,8; Wiring=Isolating switch
- GWR5273 - ROAD 5 MED.ST.AL.3M 4000K 700mA OPT.W: Catalogue Range=ROAD [5]; Colour temperature=4000 K (CRI 70); Colour temperature:=4000 K (CRI 70); Descrizione=ROAD 5 MED.ST.AL.3M 4000K 700mA OPT.W; EAN code=8011564858268; Electrocod=244C; LED LifeTime (L80B05)=77000H; LED current.=0,7A; Lamp-=LED; Lumen output (lm)=7860; Maximum surface exposed to the wind=0,19M2; Minimum distance from the illuminated object=1M; Modello=GWR5273; No. Chorus modules=3 (3x3 LED); Nominal flux (lm)=9360; Number of modules=3 (3x3 LED); Operating temperature:=-25 +50 °C; Optic=W - ULOR: 0%; Overvoltage resistance=12 KV (Common and dfferential mode); Pilot current=0,7A; SEO=Street lighting; System power=79W; Tilt adjustable=-20° ÷ +10° side bracket - -10° ÷ +20° pole head; Tipo alimentatore=Constant Current Driver Led; Tipologia=Stand alone; Voltage-=220/240 V - 50/60 Hz - Stand alone; Weight (kg)=8; Weight (kg):=8; Working temperature=-25 +50 °C
- GWR5274M30K - ROAD5 MEDI WIDE 4M 3000K 0,7A CL2 1-10V: Body=Die-cast aluminium -; Catalogue Range=ROAD [5]; Classification:=-; Color Rendering Index=CRI-70; Colore=Graphite grey; Colour :=Powder coating; Colour temperature=3000K; Colour temperature:=3000 K (CRI>80); Context=Street and parking lighting; Control System=Dimmable 1-10 V; DIN 18032-3 certification=-; Descrizione=GWR5274M30K - ROAD5 MEDI WIDE 4M 3000K 0,7A CL2 1-10V; Device with reduced surface temperature=-; Driver=Included; Driver Box=Built-in; Efficiency (lm/W)=102; Electrocod=244C; Eletrical and lighting features=-; External screw=Stainless steel; Fixing=Pole Head - Outreach; Gasket=Anti-aging silicone; General information=-; Glow Wire Test :=-; IPEA=ROAD = A + // LARGE AREAS = A3 + // CYCLOPEDONALS = A // GREEN AREAS = A // HISTORICAL CENTER = A4 +; Installationa and maintenance=-; LED Life Time (L80B05)=77000H; LED Maintenance=Not available; LED current.=0,7A; Lamp-=LED; Lifetime=L90B10 (Tq+25°C) = 100.000 h - L90B10 (Tq+50°C) = 50.000 h; Locking Hook=Integrated front handle; Lumen output (lm)=11000; Luminaire=LED Road Equipment; Materials=-; Maximum surface exposed to the wind=0,19M2; Maximum surface exposed to the wind :=0.19 m2; Minimum distance from the illuminated object=1M; Modello=GWR5274M30K; Mouting and installation=Pole Head - Outreach; Nominal flux (lm)=10800; Number of modules=4 (4x3 LED); Operating temperature :=-25 +50 °C; Operating temperature:=-25 +50 °C; Optic=WIDE; Optic :=Metallized polycarbonate reflector; Optic Maintenance=Not available; Optic and illuminating features=-; Overvoltage protection=DM 10KV / CM 10KV; Overvoltage resistance :=Common and dfferential mode: 10KV; Photobiological Risk Class=RG0; Power supply operation=Dimmable; Rated frequency (Hz)=50 / 60; SEO=Street lighting; Shield type=4mm thick flat tempered glass; Standard Deviation Colour Matching=SDCM = 5; Standard-=EN 60598-2-3, EN 60598-1 IEC/TR 62778; Standards and approvals=-; Stocking temperature=-; Supply voltage=220 - 240 V; System power=106W; System power :=108 W @ 0.7A; Tilt adjustable=-20° ÷ +10° side bracket - -10° ÷ +20° pole head; Tilt-=-20° ÷ +10° side bracket - -10° ÷ +20° pole head; Tipo alimentatore=Constant Current Driver Led; Tipologia=Dimmable; Type of light source=LED - Not replaceable; Unified Glare Rating=G*3 - ULOR = 0; Unique digital code (Datamatrix)=Currently not present; Voltage-=220/240 V - 50/60 Hz - Dimmable 1-10 V; Weight (kg):=8,4; Wiring=Isolating switch
- GWR5214 - ROAD 5 MED.ST.AL.4M 4000K 1A OPT.W: Catalogue Range=ROAD [5]; Colour temperature=4000 K (CRI 70); Colour temperature:=4000 K (CRI 70); Descrizione=ROAD 5 MED.ST.AL.4M 4000K 1A OPT.W; EAN code=8011564858299; Electrocod=244C; LED LifeTime (L80B05)=120000H; LED current.=1A; Lamp-=LED; Lumen output (lm)=15360; Maximum surface exposed to the wind=0,19M2; Minimum distance from the illuminated object=1M; Modello=GWR5214; No. Chorus modules=4 (4x3 LED); Nominal flux (lm)=19080; Number of modules=4 (4x3 LED); Operating temperature:=-25 +40 °C; Optic=W - ULOR: 0%; Overvoltage resistance=12 KV (Common and dfferential mode); Pilot current=1A; SEO=Street lighting; System power=151W; Tilt adjustable=-20° ÷ +10° side bracket - -10° ÷ +20° pole head; Tipo alimentatore=Constant Current Driver Led; Tipologia=Stand alone; Voltage-=220/240 V - 50/60 Hz - Stand alone; Weight (kg)=8,4; Weight (kg):=8,4; Working temperature=-25 +40 °C
- GWR5276 - ROAD 5 MED.ST.AL.6M 4000K 700mA OPT.W: Catalogue Range=ROAD [5]; Colour temperature=4000 K (CRI 70); Colour temperature:=4000 K (CRI 70); Descrizione=ROAD 5 MED.ST.AL.6M 4000K 700mA OPT.W; EAN code=8011564858428; Electrocod=244C; LED LifeTime (L80B05)=77000H; LED current.=0,7A; Lamp-=LED; Lumen output (lm)=15730; Maximum surface exposed to the wind=0,19M2; Minimum distance from the illuminated object=1M; Modello=GWR5276; No. Chorus modules=6 (6x3 LED); Nominal flux (lm)=18720; Number of modules=6 (6x3 LED); Operating temperature:=-25 +50 °C; Optic=W - ULOR: 0%; Overvoltage resistance=12 KV (Common and dfferential mode); Pilot current=0,7A; SEO=Street lighting; System power=159W; Tilt adjustable=-20° ÷ +10° side bracket - -10° ÷ +20° pole head; Tipo alimentatore=Constant Current Driver Led; Tipologia=Stand alone; Voltage-=220/240 V - 50/60 Hz - Stand alone; Weight (kg)=9.1; Weight (kg):=9,1; Working temperature=-25 +50 °C
- GWR5213 - ROAD 5 MED.ST.AL.3M 4000K 1A OPT.W: Catalogue Range=ROAD [5]; Colour temperature=4000 K (CRI 70); Colour temperature:=4000 K (CRI 70); Descrizione=ROAD 5 MED.ST.AL.3M 4000K 1A OPT.W; EAN code=8011564858275; Electrocod=244C; LED LifeTime (L80B05)=120000H; LED current.=1A; Lamp-=LED; Lumen output (lm)=11520; Maximum surface exposed to the wind=0,19M2; Minimum distance from the illuminated object=1M; Modello=GWR5213; No. Chorus modules=3 (3x3 LED); Nominal flux (lm)=14310; Number of modules=3 (3x3 LED); Operating temperature:=-25 +40 °C; Optic=W - ULOR: 0%; Overvoltage resistance=12 KV (Common and dfferential mode); Pilot current=1A; SEO=Street lighting; System power=113W; Tilt adjustable=-20° ÷ +10° side bracket - -10° ÷ +20° pole head; Tipo alimentatore=Constant Current Driver Led; Tipologia=Stand alone; Voltage-=220/240 V - 50/60 Hz - Stand alone; Weight (kg)=8; Weight (kg):=8; Working temperature=-25 +40 °C
- GWR5276M - ROAD5 MEDI WIDE 6M 4000K 0,7A CL2 1-10V: Catalogue Range=ROAD [5]; Colour temperature=4000 K (CRI 70); Colour temperature:=4000 K (CRI 70); Descrizione=ROAD 5 MED.DIMM.6M 4000K 700mA OPT.W; EAN code=8011564858695; Electrocod=244C; LED LifeTime (L80B05)=77000H; LED current.=0,7A; Lamp-=LED; Lumen output (lm)=15730; Maximum surface exposed to the wind=0,19M2; Minimum distance from the illuminated object=1M; Modello=GWR5276M; No. Chorus modules=6 (6x3 LED); Nominal flux (lm)=18720; Number of modules=6 (6x3 LED); Operating temperature:=-25 +50 °C; Optic=W - ULOR: 0%; Overvoltage resistance=12 KV (Common and dfferential mode); Pilot current=0,7A; Power supply operation=Dimmable; SEO=Street lighting; System power=159W; Tilt adjustable=-20° ÷ +10° side bracket - -10° ÷ +20° pole head; Tipo alimentatore=Constant Current Driver Led; Tipologia=Dimmable; Voltage-=220/240 V - 50/60 Hz - Dimmable 1-10 V; Weight (kg)=9.1; Weight (kg):=9,1; Working temperature=-25 +50 °C
- GWR5255B - ROAD5 MEDI WIDE 5M 4000K 0,5A CL2 BIREG: Body=Die-cast aluminium -; Catalogue Range=ROAD [5]; Classification:=-; Color Rendering Index=CRI-70; Colore=Graphite grey; Colour :=Powder coating; Colour temperature=4000K; Colour temperature:=4000 K (CRI>70); Context=Street and parking lighting; Control System=Bi-power with self-learning; DIN 18032-3 certification=-; Descrizione=GWR5255B - ROAD5 MEDI WIDE 5M 4000K 0,5A CL2 BIREG; Device with reduced surface temperature=-; Driver=Included; Driver Box=Built-in; Efficiency (lm/W)=124; Electrocod=244C; Eletrical and lighting features=-; External screw=Stainless steel; Fixing=Pole Head - Outreach; Gasket=Anti-aging silicone; General information=-; Glow Wire Test :=-; IPEA=ROAD = A3 + // LARGE AREAS = A6 + // CYCLOPEDONALS = A3 + // GREEN AREAS = A3 + // HISTORICAL CENTER = A6 +; Installationa and maintenance=-; LED Life Time (L80B05)=120000H; LED Maintenance=Not available; LED current.=0,5A; Lamp-=LED; Lifetime=L90B10 (Tq+25°C) = 100.000 h - L90B10 (Tq+50°C) = 50.000 h; Locking Hook=Integrated front handle; Lumen output (lm)=11700; Luminaire=LED Road Equipment; Materials=-; Maximum surface exposed to the wind=0,19M2; Maximum surface exposed to the wind :=0.19 m2; Minimum distance from the illuminated object=1M; Modello=GWR5255B; Mouting and installation=Pole Head - Outreach; Nominal flux (lm)=12000; Number of modules=5 (5x3 LED); Operating temperature :=-25 +50 °C; Operating temperature:=-25 +40 °C; Optic=WIDE; Optic :=Metallized polycarbonate reflector; Optic Maintenance=Not available; Optic and illuminating features=-; Overvoltage protection=DM 10KV / CM 10KV; Photobiological Risk Class=RG0; Power supply operation=Bi power; Rated frequency (Hz)=50 / 60; SEO=Street lighting; Shield type=4mm thick flat tempered glass; Standard Deviation Colour Matching=SDCM = 5; Standard-=EN 60598-2-3, EN 60598-1 IEC/TR 62778; Standards and approvals=-; Stocking temperature=-; Supply voltage=220 - 240 V; System power=91W; System power :=94 W @ 0.5A; Tilt adjustable=-20° ÷ +10° side bracket - -10° ÷ +20° pole head; Tilt-=-20° ÷ +10° side bracket - -10° ÷ +20° pole head; Type of light source=LED - Not replaceable; Unified Glare Rating=G*3 - ULOR = 0; Unique digital code (Datamatrix)=Currently not present; Voltage-=220/240 V - 50/60 Hz - Bi-power with self-learning; Weight (kg):=8,8; Wiring=Isolating switch
- GWR5216M - ROAD5 MEDI WIDE 6M 4000K 0,85A CL2 1-10V: Catalogue Range=ROAD [5]; Colour temperature=4000 K (CRI 70); Colour temperature:=4000 K (CRI 70); Descrizione=ROAD 5 MED.DIMM.6M 4000K 0,85A OTT.W; EAN code=8011564858701; Electrocod=244C; LED LifeTime (L80B05)=120000H; LED current.=0,85A; Lamp-=LED; Lumen output (lm)=19580; Maximum surface exposed to the wind=0,19M2; Minimum distance from the illuminated object=1M; Modello=GWR5216M; No. Chorus modules=6 (6x3 LED); Nominal flux (lm)=24330; Number of modules=6 (6x3 LED); Operating temperature:=-25 +40 °C; Optic=W - ULOR: 0%; Overvoltage resistance=12 KV (Common and dfferential mode); Pilot current=0,85A; Power supply operation=Dimmable; SEO=Street lighting; System power=185W; Tilt adjustable=-20° ÷ +10° side bracket - -10° ÷ +20° pole head; Tipo alimentatore=Constant Current Driver Led; Tipologia=Dimmable; Voltage-=220/240 V - 50/60 Hz - Dimmable 1-10 V; Weight (kg)=9.1; Weight (kg):=9,1; Working temperature=-25 +40 °C
- GWR5216B - ROAD5 MEDI WIDE 6M 4000K 0,85A CL2 BIREG: Catalogue Range=ROAD [5]; Colour temperature=4000 K (CRI 70); Colour temperature:=4000 K (CRI 70); Descrizione=ROAD 5 MED.BIPOW.6M 4000K 0,85A OPT.W; EAN code=8011564858626; Electrocod=244C; LED LifeTime (L80B05)=120000H; LED current.=0,85A; Lamp-=LED; Lumen output (lm)=19580; Maximum surface exposed to the wind=0,19M2; Minimum distance from the illuminated object=1M; Modello=GWR5216B; No. Chorus modules=6 (6x3 LED); Nominal flux (lm)=24330; Number of modules=6 (6x3 LED); Operating temperature:=-25 +40 °C; Optic=W - ULOR: 0%; Overvoltage resistance=12 KV (Common and dfferential mode); Pilot current=0,85A; Power supply operation=Bi power; SEO=Street lighting; System power=187W; Tilt adjustable=-20° ÷ +10° side bracket - -10° ÷ +20° pole head; Tipo alimentatore=Constant Current Driver Led; Tipologia=Bi power; Voltage-=220/240 V - 50/60 Hz - Bi-power with self-learning; Weight (kg)=9.1; Weight (kg):=9,1; Working temperature=-25 +40 °C
- GWR5213V - ROAD5 MEDI V.WIDE 3M 4000K 1,0A CL2: Body=Die-cast aluminium -; Catalogue Range=ROAD [5]; Classification:=-; Color Rendering Index=CRI-70; Colore=Graphite grey; Colour :=Powder coating; Colour temperature=4000K; Colour temperature:=4000 K (CRI>70); Context=Street and parking lighting; Control System=DALI - 5 Step; DIN 18032-3 certification=-; Descrizione=GWR5213V - ROAD5 MEDI V.WIDE 3M 4000K 1,0A CL2; Device with reduced surface temperature=-; Driver=Included; Driver Box=Built-in; Efficiency (lm/W)=111; Electrocod=244C; Eletrical and lighting features=-; External screw=Stainless steel; Fixing=Pole Head - Outreach; Gasket=Anti-aging silicone; General information=-; Glow Wire Test :=-; IPEA=ROAD = A ++ // LARGE AREAS = A4 + // CYCLOPEDONALS = A ++ // GREEN AREAS = A ++ // HISTORICAL CENTER = A6 +; Installationa and maintenance=-; LED Life Time (L80B05)=120000H; LED Maintenance=Not available; LED current.=1A; Lamp-=LED; Lifetime=L90B10 (Tq+25°C) = 100.000 h - L90B10 (Tq+40°C) = 75.000 h; Locking Hook=Integrated front handle; Lumen output (lm)=12800; Luminaire=LED Road Equipment; Materials=-; Maximum surface exposed to the wind=0,19M2; Maximum surface exposed to the wind :=0.19 m2; Minimum distance from the illuminated object=1M; Modello=GWR5213V; Mouting and installation=Pole Head - Outreach; Nominal flux (lm)=14310; Number of modules=3 (3x3 LED); Operating temperature :=-25 +40 °C; Operating temperature:=-25 +40 °C; Optic=WIDE; Optic :=Metallized polycarbonate reflector; Optic Maintenance=Not available; Optic and illuminating features=-; Overvoltage protection=DM 10KV / CM 10KV; Photobiological Risk Class=RG0; Rated frequency (Hz)=50 / 60; SEO=Street lighting; Shield type=4mm thick flat tempered glass; Standard Deviation Colour Matching=SDCM = 5; Standard-=EN 60598-2-3, EN 60598-1 IEC/TR 62778; Standards and approvals=-; Stocking temperature=-; Supply voltage=220 - 240 V; System power=113W; System power :=115 W @ 1A; Tilt adjustable=-20° ÷ +10° side bracket - -10° ÷ +20° pole head; Tilt-=-20° ÷ +10° side bracket - -10° ÷ +20° pole head; Tipologia=Programmable (5 step); Type of light source=LED - Not replaceable; Unified Glare Rating=G*3 - ULOR = 0; Unique digital code (Datamatrix)=Currently not present; Voltage-=220/240 V - 50/60 Hz - Stand alone and/or programmable; Weight (kg):=8; Wiring=Isolating switch
- GWR5273B30K - ROAD5 MEDI WIDE 3M 3000K 0,7A CL2 BIREG: Body=Die-cast aluminium -; Catalogue Range=ROAD [5]; Classification:=-; Color Rendering Index=CRI-70; Colore=Graphite grey; Colour :=Powder coating; Colour temperature=3000K; Colour temperature:=3000 K (CRI>80); Context=Street and parking lighting; Control System=Bi-power with self-learning; DIN 18032-3 certification=-; Descrizione=GWR5273B30K - ROAD5 MEDI WIDE 3M 3000K 0,7A CL2 BIREG; Device with reduced surface temperature=-; Driver=Included; Driver Box=Built-in; Efficiency (lm/W)=102; Electrocod=244C; Eletrical and lighting features=-; External screw=Stainless steel; Fixing=Pole Head - Outreach; Gasket=Anti-aging silicone; General information=-; Glow Wire Test :=-; IPEA=ROAD = A ++ // LARGE AREAS = A3 + // CYCLOPEDONALS = A + // GREEN AREAS = A + // HISTORICAL CENTER = A6 +; Installationa and maintenance=-; LED Life Time (L80B05)=77000H; LED Maintenance=Not available; LED current.=0,7A; Lamp-=LED; Lifetime=L90B10 (Tq+25°C) = 100.000 h - L90B10 (Tq+50°C) = 75.000 h; Locking Hook=Integrated front handle; Lumen output (lm)=8300; Luminaire=LED Road Equipment; Materials=-; Maximum surface exposed to the wind=0,19M2; Maximum surface exposed to the wind :=0.19 m2; Minimum distance from the illuminated object=1M; Modello=GWR5273B30K; Mouting and installation=Pole Head - Outreach; Nominal flux (lm)=8100; Number of modules=3 (3x3 LED); Operating temperature :=-25 +50 °C; Operating temperature:=-25 +50 °C; Optic=WIDE; Optic :=Metallized polycarbonate reflector; Optic Maintenance=Not available; Optic and illuminating features=-; Overvoltage protection=DM 10KV / CM 10KV; Overvoltage resistance :=Common and dfferential mode: 10KV; Photobiological Risk Class=RG0; Power supply operation=Bi power; Rated frequency (Hz)=50 / 60; SEO=Street lighting; Shield type=4mm thick flat tempered glass; Standard Deviation Colour Matching=SDCM = 5; Standard-=EN 60598-2-3, EN 60598-1 IEC/TR 62778; Standards and approvals=-; Stocking temperature=-; Supply voltage=220 - 240 V; System power=81W; System power :=81 W @ 0.7A; Tilt adjustable=-20° ÷ +10° side bracket - -10° ÷ +20° pole head; Tilt-=-20° ÷ +10° side bracket - -10° ÷ +20° pole head; Tipo alimentatore=Constant Current Driver Led; Tipologia=Bi power; Type of light source=LED - Not replaceable; Unified Glare Rating=G*3 - ULOR = 0; Unique digital code (Datamatrix)=Currently not present; Voltage-=220/240 V - 50/60 Hz - Bi-power with self-learning; Weight (kg):=8; Wiring=Isolating switch
- GWR5213D - ROAD5 MED WIDE 3M 4000K 1A CL2 DALI: Body=Die-cast aluminium -; Classification:=-; Color Rendering Index=CRI-70; Colore=Graphite grey; Colour :=Powder coating; Colour temperature=4000K; Context=Street and parking lighting; Control System=DALI; DIN 18032-3 certification=-; Descrizione=GWR5213D - ROAD5 MED WIDE 3M 4000K 1A CL2 DALI; Device with reduced surface temperature=-; Driver=Included; Driver Box=Built-in; Efficiency (lm/W)=111; Eletrical and lighting features=-; External screw=Stainless steel; Fixing=Pole Head - Outreach; Gasket=Anti-aging silicone; General information=-; Glow Wire Test :=-; IPEA=ROAD = A ++ // LARGE AREAS = A4 + // CYCLOPEDONALS = A ++ // GREEN AREAS = A ++ // HISTORICAL CENTER = A6 +; Installationa and maintenance=-; LED Maintenance=Not available; Lifetime=L90B10 (Tq+25°C) = 100.000 h - L90B10 (Tq+40°C) = 75.000 h; Locking Hook=Integrated front handle; Lumen output (lm)=12800; Luminaire=LED Road Equipment; Materials=-; Maximum surface exposed to the wind :=0.19 m2; Modello=GWR5213D; Mouting and installation=Pole Head - Outreach; Number of modules=3 (3x3 LED); Operating temperature :=-25 +40 °C; Optic=WIDE; Optic :=Metallized polycarbonate reflector; Optic Maintenance=Not available; Optic and illuminating features=-; Overvoltage protection=DM 10KV / CM 10KV; Photobiological Risk Class=RG0; Rated frequency (Hz)=50 / 60; Shield type=4mm thick flat tempered glass; Standard Deviation Colour Matching=SDCM = 5; Standard-=EN 60598-2-3, EN 60598-1 IEC/TR 62778; Standards and approvals=-; Stocking temperature=-; Supply voltage=220 - 240 V; System power :=115 W @ 1A; Tilt-=-20° ÷ +10° side bracket - -10° ÷ +20° pole head; Type of light source=LED - Not replaceable; Unified Glare Rating=G*3 - ULOR = 0; Unique digital code (Datamatrix)=Currently not present; Weight (kg):=8; Wiring=Isolating switch
- GWR5216B30K - ROAD5 MEDI WIDE 6M 3000K 0,85A CL2 BIREG: Body=Die-cast aluminium -; Catalogue Range=ROAD [5]; Classification:=-; Color Rendering Index=CRI-70; Colore=Graphite grey; Colour :=Powder coating; Colour temperature=3000K; Colour temperature:=3000 K (CRI>80); Context=Street and parking lighting; Control System=Bi-power with self-learning; DIN 18032-3 certification=-; Descrizione=GWR5216B30K - ROAD5 MEDI WIDE 6M 3000K 0,85A CL2 BIREG; Device with reduced surface temperature=-; Driver=Included; Driver Box=Built-in; Efficiency (lm/W)=104; Electrocod=244C; Eletrical and lighting features=-; External screw=Stainless steel; Fixing=Pole Head - Outreach; Gasket=Anti-aging silicone; General information=-; Glow Wire Test :=-; IPEA=ROAD = B // LARGE AREAS = A ++ // CYCLOPEDONALS = A // GREEN AREAS = A // HISTORICAL CENTER = A3 +; Installationa and maintenance=-; LED Life Time (L80B05)=120000H; LED Maintenance=Not available; LED current.=0,849999999999999A; Lamp-=LED; Lifetime=L90B10 (Tq+25°C) = 100.000 h - L90B10 (Tq+40°C) = 50.000 h; Locking Hook=Integrated front handle; Lumen output (lm)=19400; Luminaire=LED Road Equipment; Materials=-; Maximum surface exposed to the wind=0,19M2; Maximum surface exposed to the wind :=0.19 m2; Minimum distance from the illuminated object=1M; Modello=GWR5216B30K; Mouting and installation=Pole Head - Outreach; Nominal flux (lm)=21114; Number of modules=6 (6x3 LED); Operating temperature :=-25 +40 °C; Operating temperature:=-25 +40 °C; Optic=WIDE; Optic :=Metallized polycarbonate reflector; Optic Maintenance=Not available; Optic and illuminating features=-; Overvoltage protection=DM 10KV / CM 10KV; Overvoltage resistance :=Common and dfferential mode: 10KV; Photobiological Risk Class=RG0; Power supply operation=Bi power; Rated frequency (Hz)=50 / 60; SEO=Street lighting; Shield type=4mm thick flat tempered glass; Standard Deviation Colour Matching=SDCM = 5; Standard-=EN 60598-2-3, EN 60598-1 IEC/TR 62778; Standards and approvals=-; Stocking temperature=-; Supply voltage=220 - 240 V; System power=187W; System power :=187 W @ 0.85A; Tilt adjustable=-20° ÷ +10° side bracket - -10° ÷ +20° pole head; Tilt-=-20° ÷ +10° side bracket - -10° ÷ +20° pole head; Tipo alimentatore=Constant Current Driver Led; Tipologia=Bi power; Type of light source=LED - Not replaceable; Unified Glare Rating=G*3 - ULOR = 0; Unique digital code (Datamatrix)=Currently not present; Voltage-=220/240 V - 50/60 Hz - Bi-power with self-learning; Weight (kg):=9,09999999999999; Wiring=Isolating switch
- GWR5215B30K - ROAD5 MEDI WIDE 5M 3000K 0,85A CL2 BIREG: Body=Die-cast aluminium -; Catalogue Range=ROAD [5]; Classification:=-; Color Rendering Index=CRI-70; Colore=Graphite grey; Colour :=Powder coating; Colour temperature=3000K; Colour temperature:=3000 K (CRI>80); Context=Street and parking lighting; Control System=Bi-power with self-learning; DIN 18032-3 certification=-; Descrizione=GWR5215B30K - ROAD5 MEDI WIDE 5M 3000K 0,85A CL2 BIREG; Device with reduced surface temperature=-; Driver=Included; Driver Box=Built-in; Efficiency (lm/W)=101; Electrocod=244C; Eletrical and lighting features=-; External screw=Stainless steel; Fixing=Pole Head - Outreach; Gasket=Anti-aging silicone; General information=-; Glow Wire Test :=-; IPEA=ROAD = A // LARGE AREAS = A ++ // CYCLOPEDONALS = A // GREEN AREAS = A // HISTORICAL CENTER = A4 +; Installationa and maintenance=-; LED Life Time (L80B05)=120000H; LED Maintenance=Not available; LED current.=0,849999999999999A; Lamp-=LED; Lifetime=L90B10 (Tq+25°C) = 100.000 h - L90B10 (Tq+40°C) = 50.000 h; Locking Hook=Integrated front handle; Lumen output (lm)=16200; Luminaire=LED Road Equipment; Materials=-; Maximum surface exposed to the wind=0,19M2; Maximum surface exposed to the wind :=0.19 m2; Minimum distance from the illuminated object=1M; Modello=GWR5215B30K; Mouting and installation=Pole Head - Outreach; Nominal flux (lm)=18423; Number of modules=5 (5x3 LED); Operating temperature :=-25 +40 °C; Operating temperature:=-25 +40 °C; Optic=WIDE; Optic :=Metallized polycarbonate reflector; Optic Maintenance=Not available; Optic and illuminating features=-; Overvoltage protection=DM 10KV / CM 10KV; Overvoltage resistance :=Common and dfferential mode: 10KV; Photobiological Risk Class=RG0; Power supply operation=Bi power; Rated frequency (Hz)=50 / 60; SEO=Street lighting; Shield type=4mm thick flat tempered glass; Standard Deviation Colour Matching=SDCM = 5; Standard-=EN 60598-2-3, EN 60598-1 IEC/TR 62778; Standards and approvals=-; Stocking temperature=-; Supply voltage=220 - 240 V; System power=161W; System power :=161 W @ 0.85A; Tilt adjustable=-20° ÷ +10° side bracket - -10° ÷ +20° pole head; Tilt-=-20° ÷ +10° side bracket - -10° ÷ +20° pole head; Tipo alimentatore=Constant Current Driver Led; Tipologia=Bi power; Type of light source=LED - Not replaceable; Unified Glare Rating=G*3 - ULOR = 0; Unique digital code (Datamatrix)=Currently not present; Voltage-=220/240 V - 50/60 Hz - Bi-power with self-learning; Weight (kg):=8,8; Wiring=Isolating switch
- GWR5214M30K - ROAD5 MEDI WIDE 4M 3000K 1,0A CL2 1-10V: Body=Die-cast aluminium -; Catalogue Range=ROAD [5]; Classification:=-; Color Rendering Index=CRI-70; Colore=Graphite grey; Colour :=Powder coating; Colour temperature=3000K; Colour temperature:=3000 K (CRI>80); Context=Street and parking lighting; Control System=Dimmable 1-10 V; DIN 18032-3 certification=-; Descrizione=GWR5214M30K - ROAD5 MEDI WIDE 4M 3000K 1,0A CL2 1-10V; Device with reduced surface temperature=-; Driver=Included; Driver Box=Built-in; Efficiency (lm/W)=97; Electrocod=244C; Eletrical and lighting features=-; External screw=Stainless steel; Fixing=Pole Head - Outreach; Gasket=Anti-aging silicone; General information=-; Glow Wire Test :=-; IPEA=ROAD = B // LARGE AREAS = A ++ // CYCLOPEDONALS = B // GREEN AREAS = B // HISTORICAL CENTER = A3 +; Installationa and maintenance=-; LED Life Time (L80B05)=120000H; LED Maintenance=Not available; LED current.=1A; Lamp-=LED; Lifetime=L90B10 (Tq+25°C) = 100.000 h - L90B10 (Tq+40°C) = 50.000 h; Locking Hook=Integrated front handle; Lumen output (lm)=14800; Luminaire=LED Road Equipment; Materials=-; Maximum surface exposed to the wind=0,19M2; Maximum surface exposed to the wind :=0.19 m2; Minimum distance from the illuminated object=1M; Modello=GWR5214M30K; Mouting and installation=Pole Head - Outreach; Nominal flux (lm)=16560; Number of modules=4 (4x3 LED); Operating temperature :=-25 +40 °C; Operating temperature:=-25 +40 °C; Optic=WIDE; Optic :=Metallized polycarbonate reflector; Optic Maintenance=Not available; Optic and illuminating features=-; Overvoltage protection=DM 10KV / CM 10KV; Overvoltage resistance :=Common and dfferential mode: 10KV; Photobiological Risk Class=RG0; Power supply operation=Dimmable; Rated frequency (Hz)=50 / 60; SEO=Street lighting; Shield type=4mm thick flat tempered glass; Standard Deviation Colour Matching=SDCM = 5; Standard-=EN 60598-2-3, EN 60598-1 IEC/TR 62778; Standards and approvals=-; Stocking temperature=-; Supply voltage=220 - 240 V; System power=113W; System power :=153 W @ 1A; Tilt adjustable=-20° ÷ +10° side bracket - -10° ÷ +20° pole head; Tilt-=-20° ÷ +10° side bracket - -10° ÷ +20° pole head; Tipo alimentatore=Constant Current Driver Led; Tipologia=Dimmable; Type of light source=LED - Not replaceable; Unified Glare Rating=G*3 - ULOR = 0; Unique digital code (Datamatrix)=Currently not present; Voltage-=220/240 V - 50/60 Hz - Dimmable 1-10 V; Weight (kg):=8,4; Wiring=Isolating switch
- GWR5215M - ROAD5 MEDI WIDE 5M 4000K 0,85A CL2 1-10V: Catalogue Range=ROAD [5]; Colour temperature=4000 K (CRI 70); Colour temperature:=4000 K (CRI 70); Descrizione=ROAD 5 MED.DIMM.5M 4000K 0,85A OPT.W; EAN code=8011564858688; Electrocod=244C; LED LifeTime (L80B05)=120000H; LED current.=0,85A; Lamp-=LED; Lumen output (lm)=17090; Maximum surface exposed to the wind=0,19M2; Minimum distance from the illuminated object=1M; Modello=GWR5215M; No. Chorus modules=5 (5x3 LED); Nominal flux (lm)=21230; Number of modules=5 (5x3 LED); Operating temperature:=-25 +40 °C; Optic=W - ULOR: 0%; Overvoltage resistance=12 KV (Common and dfferential mode); Pilot current=0,85A; Power supply operation=Dimmable; SEO=Street lighting; System power=159W; Tilt adjustable=-20° ÷ +10° side bracket - -10° ÷ +20° pole head; Tipo alimentatore=Constant Current Driver Led; Tipologia=Dimmable; Voltage-=220/240 V - 50/60 Hz - Dimmable 1-10 V; Weight (kg)=8,8; Weight (kg):=8,8; Working temperature=-25 +40 °C
- GWR5213B30K - ROAD5 MEDI WIDE 3M 3000K 1,0A CL2 BIREG: Body=Die-cast aluminium -; Catalogue Range=ROAD [5]; Classification:=-; Color Rendering Index=CRI-70; Colore=Graphite grey; Colour :=Powder coating; Colour temperature=3000K; Colour temperature:=3000 K (CRI>80); Context=Street and parking lighting; Control System=Bi-power with self-learning; DIN 18032-3 certification=-; Descrizione=GWR5213B30K - ROAD5 MEDI WIDE 3M 3000K 1,0A CL2 BIREG; Device with reduced surface temperature=-; Driver=Included; Driver Box=Built-in; Efficiency (lm/W)=97; Electrocod=244C; Eletrical and lighting features=-; External screw=Stainless steel; Fixing=Pole Head - Outreach; Gasket=Anti-aging silicone; General information=-; Glow Wire Test :=-; IPEA=ROAD = A // LARGE AREAS = A ++ // CYCLOPEDONALS = A // GREEN AREAS = A // HISTORICAL CENTER = A3 +; Installationa and maintenance=-; LED Life Time (L80B05)=120000H; LED Maintenance=Not available; LED current.=1A; Lamp-=LED; Lifetime=L90B10 (Tq+25°C) = 100.000 h - L90B10 (Tq+40°C) = 75.000 h; Locking Hook=Integrated front handle; Lumen output (lm)=11100; Luminaire=LED Road Equipment; Materials=-; Maximum surface exposed to the wind=0,19M2; Maximum surface exposed to the wind :=0.19 m2; Minimum distance from the illuminated object=1M; Modello=GWR5213B30K; Mouting and installation=Pole Head - Outreach; Nominal flux (lm)=12420; Number of modules=3 (3x3 LED); Operating temperature :=-25 +40 °C; Operating temperature:=-25 +40 °C; Optic=WIDE; Optic :=Metallized polycarbonate reflector; Optic Maintenance=Not available; Optic and illuminating features=-; Overvoltage protection=DM 10KV / CM 10KV; Overvoltage resistance :=Common and dfferential mode: 10KV; Photobiological Risk Class=RG0; Power supply operation=Bi power; Rated frequency (Hz)=50 / 60; SEO=Street lighting; Shield type=4mm thick flat tempered glass; Standard Deviation Colour Matching=SDCM = 5; Standard-=EN 60598-2-3, EN 60598-1 IEC/TR 62778; Standards and approvals=-; Stocking temperature=-; Supply voltage=220 - 240 V; System power=115W; System power :=115 W @ 1A; Tilt adjustable=-20° ÷ +10° side bracket - -10° ÷ +20° pole head; Tilt-=-20° ÷ +10° side bracket - -10° ÷ +20° pole head; Tipo alimentatore=Constant Current Driver Led; Tipologia=Bi power; Type of light source=LED - Not replaceable; Unified Glare Rating=G*3 - ULOR = 0; Unique digital code (Datamatrix)=Currently not present; Voltage-=220/240 V - 50/60 Hz - Bi-power with self-learning; Weight (kg):=8; Wiring=Isolating switch
- GWR5275M - ROAD5 MEDI WIDE 5M 4000K 0,7A CL2 1-10V: Catalogue Range=ROAD [5]; Colour temperature=4000 K (CRI 70); Colour temperature:=4000 K (CRI 70); Descrizione=ROAD 5 MED.DIMM.5M 4000K 700mA OPT.W; EAN code=8011564858671; Electrocod=244C; LED LifeTime (L80B05)=77000H; LED current.=0,7A; Lamp-=LED; Lumen output (lm)=13100; Maximum surface exposed to the wind=0,19M2; Minimum distance from the illuminated object=1M; Modello=GWR5275M; No. Chorus modules=5 (5x3 LED); Nominal flux (lm)=15600; Number of modules=5 (5x3 LED); Operating temperature:=-25 +50 °C; Optic=W - ULOR: 0%; Overvoltage resistance=12 KV (Common and dfferential mode); Pilot current=0,7A; Power supply operation=Dimmable; SEO=Street lighting; System power=132W; Tilt adjustable=-20° ÷ +10° side bracket - -10° ÷ +20° pole head; Tipo alimentatore=Constant Current Driver Led; Tipologia=Dimmable; Voltage-=220/240 V - 50/60 Hz - Dimmable 1-10 V; Weight (kg)=8,8; Weight (kg):=8,8; Working temperature=-25 +50 °C
- GWR5273B - ROAD5 MEDI WIDE 3M 4000K 0,7A CL2 BIREG: Catalogue Range=ROAD [5]; Colour temperature=4000 K (CRI 70); Colour temperature:=4000 K (CRI 70); Descrizione=ROAD 5 MED.BIPOW.3M 4000K 700mA OPT.W; EAN code=8011564858442; Electrocod=244C; LED LifeTime (L80B05)=77000H; LED current.=0,7A; Lamp-=LED; Lumen output (lm)=7860; Maximum surface exposed to the wind=0,19M2; Minimum distance from the illuminated object=1M; Modello=GWR5273B; No. Chorus modules=3 (3x3 LED); Nominal flux (lm)=9360; Number of modules=3 (3x3 LED); Operating temperature:=-25 +50 °C; Optic=W - ULOR: 0%; Overvoltage resistance=12 KV (Common and dfferential mode); Pilot current=0,7A; Power supply operation=Bi power; SEO=Street lighting; System power=81W; Tilt adjustable=-20° ÷ +10° side bracket - -10° ÷ +20° pole head; Tipo alimentatore=Constant Current Driver Led; Tipologia=Bi power; Voltage-=220/240 V - 50/60 Hz - Bi-power with self-learning; Weight (kg)=8; Weight (kg):=8; Working temperature=-25 +50 °C
- GWR5255D - ROAD5 MED WIDE 5M 4000K 0,5A CL2 DALI: Body=Die-cast aluminium -; Classification:=-; Color Rendering Index=CRI-70; Colore=Graphite grey; Colour :=Powder coating; Colour temperature=4000K; Context=Street and parking lighting; Control System=DALI; DIN 18032-3 certification=-; Descrizione=GWR5255D - ROAD5 MED WIDE 5M 4000K 0,5A CL2 DALI; Device with reduced surface temperature=-; Driver=Included; Driver Box=Built-in; Efficiency (lm/W)=124; Eletrical and lighting features=-; External screw=Stainless steel; Fixing=Pole Head - Outreach; Gasket=Anti-aging silicone; General information=-; Glow Wire Test :=-; IPEA=ROAD = A3 + // LARGE AREAS = A6 + // CYCLOPEDONALS = A3 + // GREEN AREAS = A3 + // HISTORICAL CENTER = A6 +; Installationa and maintenance=-; LED Maintenance=Not available; Lifetime=L90B10 (Tq+25°C) = 100.000 h - L90B10 (Tq+50°C) = 50.000 h; Locking Hook=Integrated front handle; Lumen output (lm)=11700; Luminaire=LED Road Equipment; Materials=-; Maximum surface exposed to the wind :=0.19 m2; Modello=GWR5255D; Mouting and installation=Pole Head - Outreach; Number of modules=5 (5x3 LED); Operating temperature :=-25 +50 °C; Optic=WIDE; Optic :=Metallized polycarbonate reflector; Optic Maintenance=Not available; Optic and illuminating features=-; Overvoltage protection=DM 10KV / CM 10KV; Photobiological Risk Class=RG0; Rated frequency (Hz)=50 / 60; SEO=Street lighting; Shield type=4mm thick flat tempered glass; Standard Deviation Colour Matching=SDCM = 5; Standard-=EN 60598-2-3, EN 60598-1 IEC/TR 62778; Standards and approvals=-; Stocking temperature=-; Supply voltage=220 - 240 V; System power :=94 W @ 0.5A; Tilt-=-20° ÷ +10° side bracket - -10° ÷ +20° pole head; Type of light source=LED - Not replaceable; Unified Glare Rating=G*3 - ULOR = 0; Unique digital code (Datamatrix)=Currently not present; Weight (kg):=8,8; Wiring=Isolating switch
- GWR527630K - ROAD5 MEDI WIDE 6M 3000K 0,7A CL2: Body=Die-cast aluminium -; Catalogue Range=ROAD [5]; Classification:=-; Color Rendering Index=CRI-70; Colore=Graphite grey; Colour :=Powder coating; Colour temperature=3000K; Colour temperature:=3000 K (CRI>80); Context=Street and parking lighting; Control System=Stand alone; DIN 18032-3 certification=-; Descrizione=GWR527630K - ROAD5 MEDI WIDE 6M 3000K 0,7A CL2; Device with reduced surface temperature=-; Driver=Included; Driver Box=Built-in; Efficiency (lm/W)=104; Electrocod=244C; Eletrical and lighting features=-; External screw=Stainless steel; Fixing=Pole Head - Outreach; Gasket=Anti-aging silicone; General information=-; Glow Wire Test :=-; IPEA=ROAD = A // LARGE AREAS = A3 + // CYCLOPEDONALS = A // GREEN AREAS = A // HISTORICAL CENTER = A4 +; Installationa and maintenance=-; LED Life Time (L80B05)=77000H; LED Maintenance=Not available; LED current.=0,7A; Lamp-=LED; Lifetime=L90B10 (Tq+25°C) = 100.000 h - L90B10 (Tq+50°C) = 50.000 h; Locking Hook=Integrated front handle; Lumen output (lm)=16500; Luminaire=LED Road Equipment; Materials=-; Maximum surface exposed to the wind=0,19M2; Maximum surface exposed to the wind :=0.19 m2; Minimum distance from the illuminated object=1M; Modello=GWR527630K; Mouting and installation=Pole Head - Outreach; Nominal flux (lm)=16200; Number of modules=6 (6x3 LED); Operating temperature :=-25 +50 °C; Operating temperature:=-25 +50 °C; Optic=WIDE; Optic :=Metallized polycarbonate reflector; Optic Maintenance=Not available; Optic and illuminating features=-; Overvoltage protection=DM 10KV / CM 10KV; Overvoltage resistance :=Common and dfferential mode: 10KV; Photobiological Risk Class=RG0; Rated frequency (Hz)=50 / 60; SEO=Street lighting; Shield type=4mm thick flat tempered glass; Standard Deviation Colour Matching=SDCM = 5; Standard-=EN 60598-2-3, EN 60598-1 IEC/TR 62778; Standards and approvals=-; Stocking temperature=-; Supply voltage=220 - 240 V; System power=159W; System power :=159 W @ 0.7A; Tilt adjustable=-20° ÷ +10° side bracket - -10° ÷ +20° pole head; Tilt-=-20° ÷ +10° side bracket - -10° ÷ +20° pole head; Tipo alimentatore=Constant Current Driver Led; Tipologia=Stand alone; Type of light source=LED - Not replaceable; Unified Glare Rating=G*3 - ULOR = 0; Unique digital code (Datamatrix)=Currently not present; Voltage-=220/240 V - 50/60 Hz - Stand alone; Weight (kg):=9,09999999999999; Wiring=Isolating switch
- GWR5254D - ROAD5 MED WIDE 4M 4000K 0,5A CL2 DALI: Body=Die-cast aluminium -; Classification:=-; Color Rendering Index=CRI-70; Colore=Graphite grey; Colour :=Powder coating; Colour temperature=4000K; Context=Street and parking lighting; Control System=DALI; DIN 18032-3 certification=-; Descrizione=GWR5254D - ROAD5 MED WIDE 4M 4000K 0,5A CL2 DALI; Device with reduced surface temperature=-; Driver=Included; Driver Box=Built-in; Efficiency (lm/W)=124; Eletrical and lighting features=-; External screw=Stainless steel; Fixing=Pole Head - Outreach; Gasket=Anti-aging silicone; General information=-; Glow Wire Test :=-; IPEA=ROAD = A5 + // LARGE AREAS = A6 + // CYCLOPEDONALS = A4 + // GREEN AREAS = A4 + // HISTORICAL CENTER = A6 +; Installationa and maintenance=-; LED Maintenance=Not available; Lifetime=L90B10 (Tq+25°C) = 100.000 h - L90B10 (Tq+50°C) = 50.000 h; Locking Hook=Integrated front handle; Lumen output (lm)=9400; Luminaire=LED Road Equipment; Materials=-; Maximum surface exposed to the wind :=0.19 m2; Modello=GWR5254D; Mouting and installation=Pole Head - Outreach; Number of modules=4 (4x3 LED); Operating temperature :=-25 +50 °C; Optic=WIDE; Optic :=Metallized polycarbonate reflector; Optic Maintenance=Not available; Optic and illuminating features=-; Overvoltage protection=DM 10KV / CM 10KV; Photobiological Risk Class=RG0; Rated frequency (Hz)=50 / 60; SEO=Street lighting; Shield type=4mm thick flat tempered glass; Standard Deviation Colour Matching=SDCM = 5; Standard-=EN 60598-2-3, EN 60598-1 IEC/TR 62778; Standards and approvals=-; Stocking temperature=-; Supply voltage=220 - 240 V; System power :=76 W @ 0.5A; Tilt-=-20° ÷ +10° side bracket - -10° ÷ +20° pole head; Type of light source=LED - Not replaceable; Unified Glare Rating=G*3 - ULOR = 0; Unique digital code (Datamatrix)=Currently not present; Weight (kg):=8,4; Wiring=Isolating switch
- GWR5255M - ROAD5 MEDI WIDE 5M 4000K 0,5A CL2 1-10V: Body=Die-cast aluminium -; Catalogue Range=ROAD [5]; Classification:=-; Color Rendering Index=CRI-70; Colore=Graphite grey; Colour :=Powder coating; Colour temperature=4000K; Colour temperature:=4000 K (CRI>70); Context=Street and parking lighting; Control System=Dimmable 1-10 V; DIN 18032-3 certification=-; Descrizione=GWR5255M - ROAD5 MEDI WIDE 5M 4000K 0,5A CL2 1-10V; Device with reduced surface temperature=-; Driver=Included; Driver Box=Built-in; Efficiency (lm/W)=124; Electrocod=244C; Eletrical and lighting features=-; External screw=Stainless steel; Fixing=Pole Head - Outreach; Gasket=Anti-aging silicone; General information=-; Glow Wire Test :=-; IPEA=ROAD = A3 + // LARGE AREAS = A6 + // CYCLOPEDONALS = A3 + // GREEN AREAS = A3 + // HISTORICAL CENTER = A6 +; Installationa and maintenance=-; LED Life Time (L80B05)=120000H; LED Maintenance=Not available; LED current.=0,5A; Lamp-=LED; Lifetime=L90B10 (Tq+25°C) = 100.000 h - L90B10 (Tq+50°C) = 50.000 h; Locking Hook=Integrated front handle; Lumen output (lm)=11700; Luminaire=LED Road Equipment; Materials=-; Maximum surface exposed to the wind=0,19M2; Maximum surface exposed to the wind :=0.19 m2; Minimum distance from the illuminated object=1M; Modello=GWR5255M; Mouting and installation=Pole Head - Outreach; Nominal flux (lm)=12000; Number of modules=5 (5x3 LED); Operating temperature :=-25 +50 °C; Operating temperature:=-25 +40 °C; Optic=WIDE; Optic :=Metallized polycarbonate reflector; Optic Maintenance=Not available; Optic and illuminating features=-; Overvoltage protection=DM 10KV / CM 10KV; Photobiological Risk Class=RG0; Rated frequency (Hz)=50 / 60; SEO=Street lighting; Shield type=4mm thick flat tempered glass; Standard Deviation Colour Matching=SDCM = 5; Standard-=EN 60598-2-3, EN 60598-1 IEC/TR 62778; Standards and approvals=-; Stocking temperature=-; Supply voltage=220 - 240 V; System power=91W; System power :=94 W @ 0.5A; Tilt adjustable=-20° ÷ +10° side bracket - -10° ÷ +20° pole head; Tilt-=-20° ÷ +10° side bracket - -10° ÷ +20° pole head; Tipologia=Dimmable; Type of light source=LED - Not replaceable; Unified Glare Rating=G*3 - ULOR = 0; Unique digital code (Datamatrix)=Currently not present; Voltage-=220/240 V - 50/60 Hz - Dimmable 1-10 V; Weight (kg):=8,8; Wiring=Isolating switch
- GWR5216V - ROAD5 MEDI V.WIDE 6M 4000K 0,85A CL2: Body=Die-cast aluminium -; Catalogue Range=ROAD [5]; Classification:=-; Color Rendering Index=CRI-70; Colore=Graphite grey; Colour :=Powder coating; Colour temperature=4000K; Colour temperature:=4000 K (CRI>70); Context=Street and parking lighting; Control System=DALI - 5 Step; DIN 18032-3 certification=-; Descrizione=GWR5216V - ROAD5 MEDI V.WIDE 6M 4000K 0,85A CL2; Device with reduced surface temperature=-; Driver=Included; Driver Box=Built-in; Efficiency (lm/W)=120; Electrocod=244C; Eletrical and lighting features=-; External screw=Stainless steel; Fixing=Pole Head - Outreach; Gasket=Anti-aging silicone; General information=-; Glow Wire Test :=-; IPEA=ROAD = A + // LARGE AREAS = A4 + // CYCLOPEDONALS = A ++ // GREEN AREAS = A ++ // HISTORICAL CENTER = A6 +; Installationa and maintenance=-; LED Life Time (L80B05)=120000H; LED Maintenance=Not available; LED current.=0,849999999999999A; Lamp-=LED; Lifetime=L90B10 (Tq+25°C) = 100.000 h - L90B10 (Tq+40°C) = 50.000 h; Locking Hook=Integrated front handle; Lumen output (lm)=22400; Luminaire=LED Road Equipment; Materials=-; Maximum surface exposed to the wind=0,19M2; Maximum surface exposed to the wind :=0.19 m2; Minimum distance from the illuminated object=1M; Modello=GWR5216V; Mouting and installation=Pole Head - Outreach; Nominal flux (lm)=24330; Number of modules=6 (6x3 LED); Operating temperature :=-25 +40 °C; Operating temperature:=-25 +40 °C; Optic=WIDE; Optic :=Metallized polycarbonate reflector; Optic Maintenance=Not available; Optic and illuminating features=-; Overvoltage protection=DM 10KV / CM 10KV; Photobiological Risk Class=RG0; Rated frequency (Hz)=50 / 60; SEO=Street lighting; Shield type=4mm thick flat tempered glass; Standard Deviation Colour Matching=SDCM = 5; Standard-=EN 60598-2-3, EN 60598-1 IEC/TR 62778; Standards and approvals=-; Stocking temperature=-; Supply voltage=220 - 240 V; System power=185W; System power :=187 W @ 0.85A; Tilt adjustable=-20° ÷ +10° side bracket - -10° ÷ +20° pole head; Tilt-=-20° ÷ +10° side bracket - -10° ÷ +20° pole head; Tipologia=Programmable (5 step); Type of light source=LED - Not replaceable; Unified Glare Rating=G*3 - ULOR = 0; Unique digital code (Datamatrix)=Currently not present; Voltage-=220/240 V - 50/60 Hz - Stand alone and/or programmable; Weight (kg):=9,09999999999999; Wiring=Isolating switch
- GWR5256M - ROAD5 MEDI WIDE 6M 4000K 0,5A CL2 1-10V: Body=Die-cast aluminium -; Catalogue Range=ROAD [5]; Classification:=-; Color Rendering Index=CRI-70; Colore=Graphite grey; Colour :=Powder coating; Colour temperature=4000K; Colour temperature:=4000 K (CRI>70); Context=Street and parking lighting; Control System=Dimmable 1-10 V; DIN 18032-3 certification=-; Descrizione=GWR5256M - ROAD5 MEDI WIDE 6M 4000K 0,5A CL2 1-10V; Device with reduced surface temperature=-; Driver=Included; Driver Box=Built-in; Efficiency (lm/W)=124; Electrocod=244C; Eletrical and lighting features=-; External screw=Stainless steel; Fixing=Pole Head - Outreach; Gasket=Anti-aging silicone; General information=-; Glow Wire Test :=-; IPEA=ROAD = A3 + // LARGE AREAS = A6 + // CYCLOPEDONALS = A3 + // GREEN AREAS = A3 + // HISTORICAL CENTER = A6 +; Installationa and maintenance=-; LED Life Time (L80B05)=120000H; LED Maintenance=Not available; LED current.=0,5A; Lamp-=LED; Lifetime=L90B10 (Tq+25°C) = 100.000 h - L90B10 (Tq+50°C) = 50.000 h; Locking Hook=Integrated front handle; Lumen output (lm)=14000; Luminaire=LED Road Equipment; Materials=-; Maximum surface exposed to the wind=0,19M2; Maximum surface exposed to the wind :=0.19 m2; Minimum distance from the illuminated object=1M; Modello=GWR5256M; Mouting and installation=Pole Head - Outreach; Nominal flux (lm)=14400; Number of modules=6 (6x3 LED); Operating temperature :=-25 +50 °C; Operating temperature:=-25 +40 °C; Optic=WIDE; Optic :=Metallized polycarbonate reflector; Optic Maintenance=Not available; Optic and illuminating features=-; Overvoltage protection=DM 10KV / CM 10KV; Photobiological Risk Class=RG0; Rated frequency (Hz)=50 / 60; SEO=Street lighting; Shield type=4mm thick flat tempered glass; Standard Deviation Colour Matching=SDCM = 5; Standard-=EN 60598-2-3, EN 60598-1 IEC/TR 62778; Standards and approvals=-; Stocking temperature=-; Supply voltage=220 - 240 V; System power=109W; System power :=113 W @ 0.5A; Tilt adjustable=-20° ÷ +10° side bracket - -10° ÷ +20° pole head; Tilt-=-20° ÷ +10° side bracket - -10° ÷ +20° pole head; Tipologia=Dimmable; Type of light source=LED - Not replaceable; Unified Glare Rating=G*3 - ULOR = 0; Unique digital code (Datamatrix)=Currently not present; Voltage-=220/240 V - 50/60 Hz - Dimmable 1-10 V; Weight (kg):=9,09999999999999; Wiring=Isolating switch
- GWR521330K - ROAD 5 MED.ST.AL.3M 3000K 1A OPT.W: Body=Die-cast aluminium -; Catalogue Range=ROAD [5]; Classification:=-; Color Rendering Index=CRI-70; Colore=Graphite grey; Colour :=Powder coating; Colour temperature=3000K; Colour temperature:=3000 K (CRI>80); Context=Street and parking lighting; Control System=Stand alone; DIN 18032-3 certification=-; Descrizione=GWR521330K - ROAD 5 MED.ST.AL.3M 3000K 1A OPT.W; Device with reduced surface temperature=-; Driver=Included; Driver Box=Built-in; Efficiency (lm/W)=98; Electrocod=244C; Eletrical and lighting features=-; External screw=Stainless steel; Fixing=Pole Head - Outreach; Gasket=Anti-aging silicone; General information=-; Glow Wire Test :=-; IPEA=ROAD = A // LARGE AREAS = A3 + // CYCLOPEDONALS = A // GREEN AREAS = A // HISTORICAL CENTER = A4 +; Installationa and maintenance=-; LED Life Time (L80B05)=120000H; LED Maintenance=Not available; LED current.=1A; Lamp-=LED; Lifetime=L90B10 (Tq+25°C) = 100.000 h - L90B10 (Tq+40°C) = 75.000 h; Locking Hook=Integrated front handle; Lumen output (lm)=11100; Luminaire=LED Road Equipment; Materials=-; Maximum surface exposed to the wind=0,19M2; Maximum surface exposed to the wind :=0.19 m2; Minimum distance from the illuminated object=1M; Modello=GWR521330K; Mouting and installation=Pole Head - Outreach; Nominal flux (lm)=12420; Number of modules=3 (3x3 LED); Operating temperature :=-25 +40 °C; Operating temperature:=-25 +40 °C; Optic=WIDE; Optic :=Metallized polycarbonate reflector; Optic Maintenance=Not available; Optic and illuminating features=-; Overvoltage protection=DM 10KV / CM 10KV; Overvoltage resistance :=Common and dfferential mode: 10KV; Photobiological Risk Class=RG0; Rated frequency (Hz)=50 / 60; SEO=Street lighting; Shield type=4mm thick flat tempered glass; Standard Deviation Colour Matching=SDCM = 5; Standard-=EN 60598-2-3, EN 60598-1 IEC/TR 62778; Standards and approvals=-; Stocking temperature=-; Supply voltage=220 - 240 V; System power=113W; System power :=113 W @ 1A; Tilt adjustable=-20° ÷ +10° side bracket - -10° ÷ +20° pole head; Tilt-=-20° ÷ +10° side bracket - -10° ÷ +20° pole head; Tipo alimentatore=Constant Current Driver Led; Tipologia=Stand alone; Type of light source=LED - Not replaceable; Unified Glare Rating=G*3 - ULOR = 0; Unique digital code (Datamatrix)=Currently not present; Voltage-=220/240 V - 50/60 Hz - Stand alone; Weight (kg):=8; Wiring=Isolating switch
- GWR5253D - ROAD5 MED WIDE 3M 4000K 0,5A CL2 DALI: Body=Die-cast aluminium -; Classification:=-; Color Rendering Index=CRI-70; Colore=Graphite grey; Colour :=Powder coating; Colour temperature=4000K; Context=Street and parking lighting; Control System=DALI; DIN 18032-3 certification=-; Descrizione=GWR5253D - ROAD5 MED WIDE 3M 4000K 0,5A CL2 DALI; Device with reduced surface temperature=-; Driver=Included; Driver Box=Built-in; Efficiency (lm/W)=121; Eletrical and lighting features=-; External screw=Stainless steel; Fixing=Pole Head - Outreach; Gasket=Anti-aging silicone; General information=-; Glow Wire Test :=-; IPEA=ROAD = A5 + // LARGE AREAS = A6 + // CYCLOPEDONALS = A5 + // GREEN AREAS = A5 + // HISTORICAL CENTER = A6 +; Installationa and maintenance=-; LED Maintenance=Not available; Lifetime=L90B10 (Tq+25°C) = 100.000 h - L90B10 (Tq+50°C) = 75.000 h; Locking Hook=Integrated front handle; Lumen output (lm)=7000; Luminaire=LED Road Equipment; Materials=-; Maximum surface exposed to the wind :=0.19 m2; Modello=GWR5253D; Mouting and installation=Pole Head - Outreach; Number of modules=3 (3x3 LED); Operating temperature :=-25 +50 °C; Optic=WIDE; Optic :=Metallized polycarbonate reflector; Optic Maintenance=Not available; Optic and illuminating features=-; Overvoltage protection=DM 10KV / CM 10KV; Photobiological Risk Class=RG0; Rated frequency (Hz)=50 / 60; SEO=Street lighting; Shield type=4mm thick flat tempered glass; Standard Deviation Colour Matching=SDCM = 5; Standard-=EN 60598-2-3, EN 60598-1 IEC/TR 62778; Standards and approvals=-; Stocking temperature=-; Supply voltage=220 - 240 V; System power :=58 W @ 0.5A; Tilt-=-20° ÷ +10° side bracket - -10° ÷ +20° pole head; Type of light source=LED - Not replaceable; Unified Glare Rating=G*3 - ULOR = 0; Unique digital code (Datamatrix)=Currently not present; Weight (kg):=8; Wiring=Isolating switch
- GWR5253D30K - ROAD5 MEDI WIDE 3M 3000K 0,5A CL2: Body=Die-cast aluminium -; Classification:=-; Color Rendering Index=CRI-70; Colore=Graphite grey; Colour :=Powder coating; Colour temperature=3000K; Context=Street and parking lighting; Control System=DALI; DIN 18032-3 certification=-; Descrizione=GWR5253D30K - ROAD5 MEDI WIDE 3M 3000K 0,5A CL2; Device with reduced surface temperature=-; Driver=Included; Driver Box=Built-in; Efficiency (lm/W)=105; Eletrical and lighting features=-; External screw=Stainless steel; Fixing=Pole Head - Outreach; Gasket=Anti-aging silicone; General information=-; Glow Wire Test :=-; IPEA=ROAD = A3 + // LARGE AREAS = A4 + // CYCLOPEDONALS = A3 + // GREEN AREAS = A3 + // HISTORICAL CENTER = A6 +; Installationa and maintenance=-; LED Maintenance=Not available; Lifetime=L90B10 (Tq+25°C) = 100.000 h - L90B10 (Tq+50°C) = 75.000 h; Locking Hook=Integrated front handle; Lumen output (lm)=6100; Luminaire=LED Road Equipment; Materials=-; Maximum surface exposed to the wind :=0.19 m2; Modello=GWR5253D30K; Mouting and installation=Pole Head - Outreach; Number of modules=3 (3x3 LED); Operating temperature :=-25 +50 °C; Optic=WIDE; Optic :=Metallized polycarbonate reflector; Optic Maintenance=Not available; Optic and illuminating features=-; Overvoltage protection=DM 10KV / CM 10KV; Photobiological Risk Class=RG0; Rated frequency (Hz)=50 / 60; SEO=Street lighting; Shield type=4mm thick flat tempered glass; Standard Deviation Colour Matching=SDCM = 5; Standard-=EN 60598-2-3, EN 60598-1 IEC/TR 62778; Standards and approvals=-; Stocking temperature=-; Supply voltage=220 - 240 V; System power :=58 W @ 0.5A; Tilt-=-20° ÷ +10° side bracket - -10° ÷ +20° pole head; Type of light source=LED - Not replaceable; Unified Glare Rating=G*3 - ULOR = 0; Unique digital code (Datamatrix)=Currently not present; Weight (kg):=8; Wiring=Isolating switch
- GWR5215V - ROAD5 MEDI V.WIDE 5M 4000K 0,85A CL2: Body=Die-cast aluminium -; Catalogue Range=ROAD [5]; Classification:=-; Color Rendering Index=CRI-70; Colore=Graphite grey; Colour :=Powder coating; Colour temperature=4000K; Colour temperature:=4000 K (CRI>70); Context=Street and parking lighting; Control System=DALI - 5 Step; DIN 18032-3 certification=-; Descrizione=GWR5215V - ROAD5 MEDI V.WIDE 5M 4000K 0,85A CL2; Device with reduced surface temperature=-; Driver=Included; Driver Box=Built-in; Efficiency (lm/W)=116; Electrocod=244C; Eletrical and lighting features=-; External screw=Stainless steel; Fixing=Pole Head - Outreach; Gasket=Anti-aging silicone; General information=-; Glow Wire Test :=-; IPEA=ROAD = A + // LARGE AREAS = A5 + // CYCLOPEDONALS = A ++ // GREEN AREAS = A ++ // HISTORICAL CENTER = A6 +; Installationa and maintenance=-; LED Life Time (L80B05)=120000H; LED Maintenance=Not available; LED current.=0,849999999999999A; Lamp-=LED; Lifetime=L90B10 (Tq+25°C) = 100.000 h - L90B10 (Tq+40°C) = 50.000 h; Locking Hook=Integrated front handle; Lumen output (lm)=18700; Luminaire=LED Road Equipment; Materials=-; Maximum surface exposed to the wind=0,19M2; Maximum surface exposed to the wind :=0.19 m2; Minimum distance from the illuminated object=1M; Modello=GWR5215V; Mouting and installation=Pole Head - Outreach; Nominal flux (lm)=21230; Number of modules=5 (5x3 LED); Operating temperature :=-25 +40 °C; Operating temperature:=-25 +40 °C; Optic=WIDE; Optic :=Metallized polycarbonate reflector; Optic Maintenance=Not available; Optic and illuminating features=-; Overvoltage protection=DM 10KV / CM 10KV; Photobiological Risk Class=RG0; Rated frequency (Hz)=50 / 60; SEO=Street lighting; Shield type=4mm thick flat tempered glass; Standard Deviation Colour Matching=SDCM = 5; Standard-=EN 60598-2-3, EN 60598-1 IEC/TR 62778; Standards and approvals=-; Stocking temperature=-; Supply voltage=220 - 240 V; System power=159W; System power :=161 W @ 0.85A; Tilt adjustable=-20° ÷ +10° side bracket - -10° ÷ +20° pole head; Tilt-=-20° ÷ +10° side bracket - -10° ÷ +20° pole head; Tipologia=Programmable (5 step); Type of light source=LED - Not replaceable; Unified Glare Rating=G*3 - ULOR = 0; Unique digital code (Datamatrix)=Currently not present; Voltage-=220/240 V - 50/60 Hz - Stand alone and/or programmable; Weight (kg):=8,8; Wiring=Isolating switch
- GWR5213B - ROAD 5 MED.BIPOW.3M 4000K 1A OPT.W: Catalogue Range=ROAD [5]; Colour temperature=4000 K (CRI 70); Colour temperature:=4000 K (CRI 70); Descrizione=ROAD 5 MED.BIPOW.3M 4000K 1A OPT.W; EAN code=8011564858459; Electrocod=244C; LED LifeTime (L80B05)=120000H; LED current.=1A; Lamp-=LED; Lumen output (lm)=11520; Maximum surface exposed to the wind=0,19M2; Minimum distance from the illuminated object=1M; Modello=GWR5213B; No. Chorus modules=3 (3x3 LED); Nominal flux (lm)=14310; Number of modules=3 (3x3 LED); Operating temperature:=-25 +40 °C; Optic=W - ULOR: 0%; Overvoltage resistance=12 KV (Common and dfferential mode); Pilot current=1A; Power supply operation=Bi power; SEO=Street lighting; System power=115W; Tilt adjustable=-20° ÷ +10° side bracket - -10° ÷ +20° pole head; Tipo alimentatore=Constant Current Driver Led; Tipologia=Bi power; Voltage-=220/240 V - 50/60 Hz - Bi-power with self-learning; Weight (kg)=8; Weight (kg):=8; Working temperature=-25 +40 °C
- GWR5273M - ROAD5 MEDI WIDE 3M 4000K 0,7A CL2 1-10V: Catalogue Range=ROAD [5]; Colour temperature=4000 K (CRI 70); Colour temperature:=4000 K (CRI 70); Descrizione=ROAD 5 MED.DIMM.3M 4000K 700mA OPT.W; EAN code=8011564858633; Electrocod=244C; LED LifeTime (L80B05)=77000H; LED current.=0,7A; Lamp-=LED; Lumen output (lm)=7860; Maximum surface exposed to the wind=0,19M2; Minimum distance from the illuminated object=1M; Modello=GWR5273M; No. Chorus modules=3 (3x3 LED); Nominal flux (lm)=9360; Number of modules=3 (3x3 LED); Operating temperature:=-25 +50 °C; Optic=W - ULOR: 0%; Overvoltage resistance=12 KV (Common and dfferential mode); Pilot current=0,7A; Power supply operation=Dimmable; SEO=Street lighting; System power=79W; Tilt adjustable=-20° ÷ +10° side bracket - -10° ÷ +20° pole head; Tipo alimentatore=Constant Current Driver Led; Tipologia=Dimmable; Voltage-=220/240 V - 50/60 Hz - Dimmable 1-10 V; Weight (kg)=8; Weight (kg):=8; Working temperature=-25 +50 °C
- GWR5255D30K - ROAD5 MEDI WIDE 5M 3000K 0,5A CL2: Body=Die-cast aluminium -; Classification:=-; Color Rendering Index=CRI-70; Colore=Graphite grey; Colour :=Powder coating; Colour temperature=3000K; Context=Street and parking lighting; Control System=DALI; DIN 18032-3 certification=-; Descrizione=GWR5255D30K - ROAD5 MEDI WIDE 5M 3000K 0,5A CL2; Device with reduced surface temperature=-; Driver=Included; Driver Box=Built-in; Efficiency (lm/W)=109; Eletrical and lighting features=-; External screw=Stainless steel; Fixing=Pole Head - Outreach; Gasket=Anti-aging silicone; General information=-; Glow Wire Test :=-; IPEA=ROAD = A ++ // LARGE AREAS = A4 + // CYCLOPEDONALS = A + // GREEN AREAS = A + // HISTORICAL CENTER = A5 +; Installationa and maintenance=-; LED Maintenance=Not available; Lifetime=L90B10 (Tq+25°C) = 100.000 h - L90B10 (Tq+50°C) = 50.000 h; Locking Hook=Integrated front handle; Lumen output (lm)=10200; Luminaire=LED Road Equipment; Materials=-; Maximum surface exposed to the wind :=0.19 m2; Modello=GWR5255D30K; Mouting and installation=Pole Head - Outreach; Number of modules=5 (5x3 LED); Operating temperature :=-25 +50 °C; Optic=WIDE; Optic :=Metallized polycarbonate reflector; Optic Maintenance=Not available; Optic and illuminating features=-; Overvoltage protection=DM 10KV / CM 10KV; Photobiological Risk Class=RG0; Rated frequency (Hz)=50 / 60; SEO=Street lighting; Shield type=4mm thick flat tempered glass; Standard Deviation Colour Matching=SDCM = 5; Standard-=EN 60598-2-3, EN 60598-1 IEC/TR 62778; Standards and approvals=-; Stocking temperature=-; Supply voltage=220 - 240 V; System power :=94 W @ 0.5A; Tilt-=-20° ÷ +10° side bracket - -10° ÷ +20° pole head; Type of light source=LED - Not replaceable; Unified Glare Rating=G*3 - ULOR = 0; Unique digital code (Datamatrix)=Currently not present; Weight (kg):=8,8; Wiring=Isolating switch
- GWR521430K - ROAD 5 MED.ST.AL.4M 3000K 1A OPT.W: Body=Die-cast aluminium -; Catalogue Range=ROAD [5]; Classification:=-; Color Rendering Index=CRI-70; Colore=Graphite grey; Colour :=Powder coating; Colour temperature=3000K; Colour temperature:=3000 K (CRI>80); Context=Street and parking lighting; Control System=Stand alone; DIN 18032-3 certification=-; Descrizione=GWR521430K - ROAD 5 MED.ST.AL.4M 3000K 1A OPT.W; Device with reduced surface temperature=-; Driver=Included; Driver Box=Built-in; Efficiency (lm/W)=98; Electrocod=244C; Eletrical and lighting features=-; External screw=Stainless steel; Fixing=Pole Head - Outreach; Gasket=Anti-aging silicone; General information=-; Glow Wire Test :=-; IPEA=ROAD = B // LARGE AREAS = A ++ // CYCLOPEDONALS = A // GREEN AREAS = A // HISTORICAL CENTER = A4 +; Installationa and maintenance=-; LED Life Time (L80B05)=120000H; LED Maintenance=Not available; LED current.=1A; Lamp-=LED; Lifetime=L90B10 (Tq+25°C) = 100.000 h - L90B10 (Tq+40°C) = 50.000 h; Locking Hook=Integrated front handle; Lumen output (lm)=14800; Luminaire=LED Road Equipment; Materials=-; Maximum surface exposed to the wind=0,19M2; Maximum surface exposed to the wind :=0.19 m2; Minimum distance from the illuminated object=1M; Modello=GWR521430K; Mouting and installation=Pole Head - Outreach; Nominal flux (lm)=16560; Number of modules=4 (4x3 LED); Operating temperature :=-25 +40 °C; Operating temperature:=-25 +40 °C; Optic=WIDE; Optic :=Metallized polycarbonate reflector; Optic Maintenance=Not available; Optic and illuminating features=-; Overvoltage protection=DM 10KV / CM 10KV; Overvoltage resistance :=Common and dfferential mode: 10KV; Photobiological Risk Class=RG0; Rated frequency (Hz)=50 / 60; SEO=Street lighting; Shield type=4mm thick flat tempered glass; Standard Deviation Colour Matching=SDCM = 5; Standard-=EN 60598-2-3, EN 60598-1 IEC/TR 62778; Standards and approvals=-; Stocking temperature=-; Supply voltage=220 - 240 V; System power=151W; System power :=151 W @ 1A; Tilt adjustable=-20° ÷ +10° side bracket - -10° ÷ +20° pole head; Tilt-=-20° ÷ +10° side bracket - -10° ÷ +20° pole head; Tipo alimentatore=Constant Current Driver Led; Tipologia=Stand alone; Type of light source=LED - Not replaceable; Unified Glare Rating=G*3 - ULOR = 0; Unique digital code (Datamatrix)=Currently not present; Voltage-=220/240 V - 50/60 Hz - Stand alone; Weight (kg):=8,4; Wiring=Isolating switch
- GWR5276B30K - ROAD5 MEDI WIDE 6M 3000K 0,7A CL2 BIREG: Body=Die-cast aluminium -; Catalogue Range=ROAD [5]; Classification:=-; Color Rendering Index=CRI-70; Colore=Graphite grey; Colour :=Powder coating; Colour temperature=3000K; Colour temperature:=3000 K (CRI>80); Context=Street and parking lighting; Control System=Bi-power with self-learning; DIN 18032-3 certification=-; Descrizione=GWR5276B30K - ROAD5 MEDI WIDE 6M 3000K 0,7A CL2 BIREG; Device with reduced surface temperature=-; Driver=Included; Driver Box=Built-in; Efficiency (lm/W)=102; Electrocod=244C; Eletrical and lighting features=-; External screw=Stainless steel; Fixing=Pole Head - Outreach; Gasket=Anti-aging silicone; General information=-; Glow Wire Test :=-; IPEA=ROAD = A // LARGE AREAS = A3 + // CYCLOPEDONALS = A // GREEN AREAS = A // HISTORICAL CENTER = A4 +; Installationa and maintenance=-; LED Life Time (L80B05)=77000H; LED Maintenance=Not available; LED current.=0,7A; Lamp-=LED; Lifetime=L90B10 (Tq+25°C) = 100.000 h - L90B10 (Tq+50°C) = 50.000 h; Locking Hook=Integrated front handle; Lumen output (lm)=16500; Luminaire=LED Road Equipment; Materials=-; Maximum surface exposed to the wind=0,19M2; Maximum surface exposed to the wind :=0.19 m2; Minimum distance from the illuminated object=1M; Modello=GWR5276B30K; Mouting and installation=Pole Head - Outreach; Nominal flux (lm)=16200; Number of modules=6 (6x3 LED); Operating temperature :=-25 +50 °C; Operating temperature:=-25 +50 °C; Optic=WIDE; Optic :=Metallized polycarbonate reflector; Optic Maintenance=Not available; Optic and illuminating features=-; Overvoltage protection=DM 10KV / CM 10KV; Overvoltage resistance :=Common and dfferential mode: 10KV; Photobiological Risk Class=RG0; Power supply operation=Bi power; Rated frequency (Hz)=50 / 60; SEO=Street lighting; Shield type=4mm thick flat tempered glass; Standard Deviation Colour Matching=SDCM = 5; Standard-=EN 60598-2-3, EN 60598-1 IEC/TR 62778; Standards and approvals=-; Stocking temperature=-; Supply voltage=220 - 240 V; System power=161W; System power :=161 W @ 0.7A; Tilt adjustable=-20° ÷ +10° side bracket - -10° ÷ +20° pole head; Tilt-=-20° ÷ +10° side bracket - -10° ÷ +20° pole head; Tipo alimentatore=Constant Current Driver Led; Tipologia=Bi power; Type of light source=LED - Not replaceable; Unified Glare Rating=G*3 - ULOR = 0; Unique digital code (Datamatrix)=Currently not present; Voltage-=220/240 V - 50/60 Hz - Bi-power with self-learning; Weight (kg):=9,09999999999999; Wiring=Isolating switch
- GWR5275M30K - ROAD5 MEDI WIDE 5M 3000K 0,7A CL2 1-10V: Body=Die-cast aluminium -; Catalogue Range=ROAD [5]; Classification:=-; Color Rendering Index=CRI-70; Colore=Graphite grey; Colour :=Powder coating; Colour temperature=3000K; Colour temperature:=3000 K (CRI>80); Context=Street and parking lighting; Control System=Dimmable 1-10 V; DIN 18032-3 certification=-; Descrizione=GWR5275M30K - ROAD5 MEDI WIDE 5M 3000K 0,7A CL2 1-10V; Device with reduced surface temperature=-; Driver=Included; Driver Box=Built-in; Efficiency (lm/W)=102; Electrocod=244C; Eletrical and lighting features=-; External screw=Stainless steel; Fixing=Pole Head - Outreach; Gasket=Anti-aging silicone; General information=-; Glow Wire Test :=-; IPEA=ROAD = A // LARGE AREAS = A3 + // CYCLOPEDONALS = A // GREEN AREAS = A // HISTORICAL CENTER = A4 +; Installationa and maintenance=-; LED Life Time (L80B05)=77000H; LED Maintenance=Not available; LED current.=0,7A; Lamp-=LED; Lifetime=L90B10 (Tq+25°C) = 100.000 h - L90B10 (Tq+50°C) = 50.000 h; Locking Hook=Integrated front handle; Lumen output (lm)=13700; Luminaire=LED Road Equipment; Materials=-; Maximum surface exposed to the wind=0,19M2; Maximum surface exposed to the wind :=0.19 m2; Minimum distance from the illuminated object=1M; Modello=GWR5275M30K; Mouting and installation=Pole Head - Outreach; Nominal flux (lm)=13500; Number of modules=5 (5x3 LED); Operating temperature :=-25 +50 °C; Operating temperature:=-25 +50 °C; Optic=WIDE; Optic :=Metallized polycarbonate reflector; Optic Maintenance=Not available; Optic and illuminating features=-; Overvoltage protection=DM 10KV / CM 10KV; Overvoltage resistance :=Common and dfferential mode: 10KV; Photobiological Risk Class=RG0; Power supply operation=Dimmable; Rated frequency (Hz)=50 / 60; SEO=Street lighting; Shield type=4mm thick flat tempered glass; Standard Deviation Colour Matching=SDCM = 5; Standard-=EN 60598-2-3, EN 60598-1 IEC/TR 62778; Standards and approvals=-; Stocking temperature=-; Supply voltage=220 - 240 V; System power=132W; System power :=134 W @ 0.7A; Tilt adjustable=-20° ÷ +10° side bracket - -10° ÷ +20° pole head; Tilt-=-20° ÷ +10° side bracket - -10° ÷ +20° pole head; Tipo alimentatore=Constant Current Driver Led; Tipologia=Dimmable; Type of light source=LED - Not replaceable; Unified Glare Rating=G*3 - ULOR = 0; Unique digital code (Datamatrix)=Currently not present; Voltage-=220/240 V - 50/60 Hz - Dimmable 1-10 V; Weight (kg):=8,8; Wiring=Isolating switch
- GWR5254D30K - ROAD5 MEDI WIDE 4M 3000K 0,5A CL2: Body=Die-cast aluminium -; Classification:=-; Color Rendering Index=CRI-70; Colore=Graphite grey; Colour :=Powder coating; Colour temperature=3000K; Context=Street and parking lighting; Control System=DALI; DIN 18032-3 certification=-; Descrizione=GWR5254D30K - ROAD5 MEDI WIDE 4M 3000K 0,5A CL2; Device with reduced surface temperature=-; Driver=Included; Driver Box=Built-in; Efficiency (lm/W)=107; Eletrical and lighting features=-; External screw=Stainless steel; Fixing=Pole Head - Outreach; Gasket=Anti-aging silicone; General information=-; Glow Wire Test :=-; IPEA=ROAD = A3 + // LARGE AREAS = A4 + // CYCLOPEDONALS = A ++ // GREEN AREAS = A ++ // HISTORICAL CENTER = A6 +; Installationa and maintenance=-; LED Maintenance=Not available; Lifetime=L90B10 (Tq+25°C) = 100.000 h - L90B10 (Tq+50°C) = 50.000 h; Locking Hook=Integrated front handle; Lumen output (lm)=8100; Luminaire=LED Road Equipment; Materials=-; Maximum surface exposed to the wind :=0.19 m2; Modello=GWR5254D30K; Mouting and installation=Pole Head - Outreach; Number of modules=4 (4x3 LED); Operating temperature :=-25 +50 °C; Optic=WIDE; Optic :=Metallized polycarbonate reflector; Optic Maintenance=Not available; Optic and illuminating features=-; Overvoltage protection=DM 10KV / CM 10KV; Photobiological Risk Class=RG0; Rated frequency (Hz)=50 / 60; SEO=Street lighting; Shield type=4mm thick flat tempered glass; Standard Deviation Colour Matching=SDCM = 5; Standard-=EN 60598-2-3, EN 60598-1 IEC/TR 62778; Standards and approvals=-; Stocking temperature=-; Supply voltage=220 - 240 V; System power :=76 W @ 0.5A; Tilt-=-20° ÷ +10° side bracket - -10° ÷ +20° pole head; Type of light source=LED - Not replaceable; Unified Glare Rating=G*3 - ULOR = 0; Unique digital code (Datamatrix)=Currently not present; Weight (kg):=8,4; Wiring=Isolating switch
- GWR5256D - ROAD5 MED WIDE 6M 4000K 0,5A CL2 DALI: Body=Die-cast aluminium -; Classification:=-; Color Rendering Index=CRI-70; Colore=Graphite grey; Colour :=Powder coating; Colour temperature=4000K; Context=Street and parking lighting; Control System=DALI; DIN 18032-3 certification=-; Descrizione=GWR5256D - ROAD5 MED WIDE 6M 4000K 0,5A CL2 DALI; Device with reduced surface temperature=-; Driver=Included; Driver Box=Built-in; Efficiency (lm/W)=124; Eletrical and lighting features=-; External screw=Stainless steel; Fixing=Pole Head - Outreach; Gasket=Anti-aging silicone; General information=-; Glow Wire Test :=-; IPEA=ROAD = A3 + // LARGE AREAS = A6 + // CYCLOPEDONALS = A3 + // GREEN AREAS = A3 + // HISTORICAL CENTER = A6 +; Installationa and maintenance=-; LED Maintenance=Not available; Lifetime=L90B10 (Tq+25°C) = 100.000 h - L90B10 (Tq+50°C) = 50.000 h; Locking Hook=Integrated front handle; Lumen output (lm)=14000; Luminaire=LED Road Equipment; Materials=-; Maximum surface exposed to the wind :=0.19 m2; Modello=GWR5256D; Mouting and installation=Pole Head - Outreach; Number of modules=6 (6x3 LED); Operating temperature :=-25 +50 °C; Optic=WIDE; Optic :=Metallized polycarbonate reflector; Optic Maintenance=Not available; Optic and illuminating features=-; Overvoltage protection=DM 10KV / CM 10KV; Photobiological Risk Class=RG0; Rated frequency (Hz)=50 / 60; Shield type=4mm thick flat tempered glass; Standard Deviation Colour Matching=SDCM = 5; Standard-=EN 60598-2-3, EN 60598-1 IEC/TR 62778; Standards and approvals=-; Stocking temperature=-; Supply voltage=220 - 240 V; System power :=113 W @ 0.5A; Tilt-=-20° ÷ +10° side bracket - -10° ÷ +20° pole head; Type of light source=LED - Not replaceable; Unified Glare Rating=G*3 - ULOR = 0; Unique digital code (Datamatrix)=Currently not present; Weight (kg):=9,09999999999999; Wiring=Isolating switch
- GWR5214B - ROAD5 MEDI WIDE 4M 4000K 1,0A CL2 BIREG: Catalogue Range=ROAD [5]; Colour temperature=4000 K (CRI 70); Colour temperature:=4000 K (CRI 70); Descrizione=ROAD 5 MED.BIPOW.4M 4000K 1A OPT.W; EAN code=8011564858480; Electrocod=244C; LED LifeTime (L80B05)=120000H; LED current.=1A; Lamp-=LED; Lumen output (lm)=15360; Maximum surface exposed to the wind=0,19M2; Minimum distance from the illuminated object=1M; Modello=GWR5214B; No. Chorus modules=4 (4x3 LED); Nominal flux (lm)=19080; Number of modules=4 (4x3 LED); Operating temperature:=-25 +40 °C; Optic=W - ULOR: 0%; Overvoltage resistance=12 KV (Common and dfferential mode); Pilot current=1A; Power supply operation=Bi power; SEO=Street lighting; System power=153W; Tilt adjustable=-20° ÷ +10° side bracket - -10° ÷ +20° pole head; Tipo alimentatore=Constant Current Driver Led; Tipologia=Bi power; Voltage-=220/240 V - 50/60 Hz - Bi-power with self-learning; Weight (kg):=8,4; Working temperature=-25 +40 °C
- GWR5273M30K - ROAD5 MEDI WIDE 3M 3000K 0,7A CL2 1-10V: Body=Die-cast aluminium -; Catalogue Range=ROAD [5]; Classification:=-; Color Rendering Index=CRI-70; Colore=Graphite grey; Colour :=Powder coating; Colour temperature=3000K; Colour temperature:=3000 K (CRI>80); Context=Street and parking lighting; Control System=Dimmable 1-10 V; DIN 18032-3 certification=-; Descrizione=GWR5273M30K - ROAD5 MEDI WIDE 3M 3000K 0,7A CL2 1-10V; Device with reduced surface temperature=-; Driver=Included; Driver Box=Built-in; Efficiency (lm/W)=102; Electrocod=244C; Eletrical and lighting features=-; External screw=Stainless steel; Fixing=Pole Head - Outreach; Gasket=Anti-aging silicone; General information=-; Glow Wire Test :=-; IPEA=ROAD = A ++ // LARGE AREAS = A3 + // CYCLOPEDONALS = A + // GREEN AREAS = A + // HISTORICAL CENTER = A6 +; Installationa and maintenance=-; LED Life Time (L80B05)=77000H; LED Maintenance=Not available; LED current.=0,7A; Lamp-=LED; Lifetime=L90B10 (Tq+25°C) = 100.000 h - L90B10 (Tq+50°C) = 75.000 h; Locking Hook=Integrated front handle; Lumen output (lm)=8300; Luminaire=LED Road Equipment; Materials=-; Maximum surface exposed to the wind=0,19M2; Maximum surface exposed to the wind :=0.19 m2; Minimum distance from the illuminated object=1M; Modello=GWR5273M30K; Mouting and installation=Pole Head - Outreach; Nominal flux (lm)=8100; Number of modules=3 (3x3 LED); Operating temperature :=-25 +50 °C; Operating temperature:=-25 +50 °C; Optic=WIDE; Optic :=Metallized polycarbonate reflector; Optic Maintenance=Not available; Optic and illuminating features=-; Overvoltage protection=DM 10KV / CM 10KV; Overvoltage resistance :=Common and dfferential mode: 10KV; Photobiological Risk Class=RG0; Power supply operation=Dimmable; Rated frequency (Hz)=50 / 60; SEO=Street lighting; Shield type=4mm thick flat tempered glass; Standard Deviation Colour Matching=SDCM = 5; Standard-=EN 60598-2-3, EN 60598-1 IEC/TR 62778; Standards and approvals=-; Stocking temperature=-; Supply voltage=220 - 240 V; System power=79W; System power :=81 W @ 0.7A; Tilt adjustable=-20° ÷ +10° side bracket - -10° ÷ +20° pole head; Tilt-=-20° ÷ +10° side bracket - -10° ÷ +20° pole head; Tipo alimentatore=Constant Current Driver Led; Tipologia=Dimmable; Type of light source=LED - Not replaceable; Unified Glare Rating=G*3 - ULOR = 0; Unique digital code (Datamatrix)=Currently not present; Voltage-=220/240 V - 50/60 Hz - Dimmable 1-10 V; Weight (kg):=8; Wiring=Isolating switch
- GWR5274M - ROAD5 MEDI WIDE 4M 4000K 0,7A CL2 1-10V: Catalogue Range=ROAD [5]; Colour temperature=4000 K (CRI 70); Colour temperature:=4000 K (CRI 70); Descrizione=ROAD 5 MED.DIMM.4M 4000K 700mA OPT.W; EAN code=8011564858657; Electrocod=244C; LED LifeTime (L80B05)=77000H; LED current.=0,7A; Lamp-=LED; Lumen output (lm)=10480; Maximum surface exposed to the wind=0,19M2; Minimum distance from the illuminated object=1M; Modello=GWR5274M; No. Chorus modules=4 (4x3 LED); Nominal flux (lm)=12480; Number of modules=4 (4x3 LED); Operating temperature:=-25 +50 °C; Optic=W - ULOR: 0%; Overvoltage resistance=12 KV (Common and dfferential mode); Pilot current=0,7A; Power supply operation=Dimmable; SEO=Street lighting; System power=106W; Tilt adjustable=-20° ÷ +10° side bracket - -10° ÷ +20° pole head; Tipo alimentatore=Constant Current Driver Led; Tipologia=Dimmable; Voltage-=220/240 V - 50/60 Hz - Dimmable 1-10 V; Weight (kg)=8,4; Weight (kg):=8,4; Working temperature=-25 +50 °C
- GWR527530K - ROAD5 MEDI WIDE 5M 3000K 0,7A CL2: Body=Die-cast aluminium -; Catalogue Range=ROAD [5]; Classification:=-; Color Rendering Index=CRI-70; Colore=Graphite grey; Colour :=Powder coating; Colour temperature=3000K; Colour temperature:=3000 K (CRI>80); Context=Street and parking lighting; Control System=Stand alone; DIN 18032-3 certification=-; Descrizione=GWR527530K - ROAD5 MEDI WIDE 5M 3000K 0,7A CL2; Device with reduced surface temperature=-; Driver=Included; Driver Box=Built-in; Efficiency (lm/W)=104; Electrocod=244C; Eletrical and lighting features=-; External screw=Stainless steel; Fixing=Pole Head - Outreach; Gasket=Anti-aging silicone; General information=-; Glow Wire Test :=-; IPEA=ROAD = A // LARGE AREAS = A3 + // CYCLOPEDONALS = A // GREEN AREAS = A // HISTORICAL CENTER = A4 +; Installationa and maintenance=-; LED Life Time (L80B05)=77000H; LED Maintenance=Not available; LED current.=0,7A; Lamp-=LED; Lifetime=L90B10 (Tq+25°C) = 100.000 h - L90B10 (Tq+50°C) = 50.000 h; Locking Hook=Integrated front handle; Lumen output (lm)=13700; Luminaire=LED Road Equipment; Materials=-; Maximum surface exposed to the wind=0,19M2; Maximum surface exposed to the wind :=0.19 m2; Minimum distance from the illuminated object=1M; Modello=GWR527530K; Mouting and installation=Pole Head - Outreach; Nominal flux (lm)=13500; Number of modules=5 (5x3 LED); Operating temperature :=-25 +50 °C; Operating temperature:=-25 +50 °C; Optic=WIDE; Optic :=Metallized polycarbonate reflector; Optic Maintenance=Not available; Optic and illuminating features=-; Overvoltage protection=DM 10KV / CM 10KV; Overvoltage resistance :=Common and dfferential mode: 10KV; Photobiological Risk Class=RG0; Rated frequency (Hz)=50 / 60; SEO=Street lighting; Shield type=4mm thick flat tempered glass; Standard Deviation Colour Matching=SDCM = 5; Standard-=EN 60598-2-3, EN 60598-1 IEC/TR 62778; Standards and approvals=-; Stocking temperature=-; Supply voltage=220 - 240 V; System power=132W; System power :=132 W @ 0.7A; Tilt adjustable=-20° ÷ +10° side bracket - -10° ÷ +20° pole head; Tilt-=-20° ÷ +10° side bracket - -10° ÷ +20° pole head; Tipo alimentatore=Constant Current Driver Led; Tipologia=Stand alone; Type of light source=LED - Not replaceable; Unified Glare Rating=G*3 - ULOR = 0; Unique digital code (Datamatrix)=Currently not present; Voltage-=220/240 V - 50/60 Hz - Stand alone; Weight (kg):=8,8; Wiring=Isolating switch
- GWR5254M - ROAD5 MEDI WIDE 4M 4000K 0,5A CL2 1-10V: Body=Die-cast aluminium -; Catalogue Range=ROAD [5]; Classification:=-; Color Rendering Index=CRI-70; Colore=Graphite grey; Colour :=Powder coating; Colour temperature=4000K; Colour temperature:=4000 K (CRI>70); Context=Street and parking lighting; Control System=Dimmable 1-10 V; DIN 18032-3 certification=-; Descrizione=GWR5254M - ROAD5 MEDI WIDE 4M 4000K 0,5A CL2 1-10V; Device with reduced surface temperature=-; Driver=Included; Driver Box=Built-in; Efficiency (lm/W)=124; Electrocod=244C; Eletrical and lighting features=-; External screw=Stainless steel; Fixing=Pole Head - Outreach; Gasket=Anti-aging silicone; General information=-; Glow Wire Test :=-; IPEA=ROAD = A5 + // LARGE AREAS = A6 + // CYCLOPEDONALS = A4 + // GREEN AREAS = A4 + // HISTORICAL CENTER = A6 +; Installationa and maintenance=-; LED Life Time (L80B05)=120000H; LED Maintenance=Not available; LED current.=0,5A; Lamp-=LED; Lifetime=L90B10 (Tq+25°C) = 100.000 h - L90B10 (Tq+50°C) = 50.000 h; Locking Hook=Integrated front handle; Lumen output (lm)=9400; Luminaire=LED Road Equipment; Materials=-; Maximum surface exposed to the wind=0,19M2; Maximum surface exposed to the wind :=0.19 m2; Minimum distance from the illuminated object=1M; Modello=GWR5254M; Mouting and installation=Pole Head - Outreach; Nominal flux (lm)=9600; Number of modules=4 (4x3 LED); Operating temperature :=-25 +50 °C; Operating temperature:=-25 +40 °C; Optic=WIDE; Optic :=Metallized polycarbonate reflector; Optic Maintenance=Not available; Optic and illuminating features=-; Overvoltage protection=DM 10KV / CM 10KV; Photobiological Risk Class=RG0; Rated frequency (Hz)=50 / 60; SEO=Street lighting; Shield type=4mm thick flat tempered glass; Standard Deviation Colour Matching=SDCM = 5; Standard-=EN 60598-2-3, EN 60598-1 IEC/TR 62778; Standards and approvals=-; Stocking temperature=-; Supply voltage=220 - 240 V; System power=73W; System power :=76 W @ 0.5A; Tilt adjustable=-20° ÷ +10° side bracket - -10° ÷ +20° pole head; Tilt-=-20° ÷ +10° side bracket - -10° ÷ +20° pole head; Tipologia=Dimmable; Type of light source=LED - Not replaceable; Unified Glare Rating=G*3 - ULOR = 0; Unique digital code (Datamatrix)=Currently not present; Voltage-=220/240 V - 50/60 Hz - Dimmable 1-10 V; Weight (kg):=8,4; Wiring=Isolating switch
- GWR5214B30K - ROAD5 MEDI WIDE 4M 3000K 1,0A CL2 BIREG: Body=Die-cast aluminium -; Catalogue Range=ROAD [5]; Classification:=-; Color Rendering Index=CRI-70; Colore=Graphite grey; Colour :=Powder coating; Colour temperature=3000K; Colour temperature:=3000 K (CRI>80); Context=Street and parking lighting; Control System=Bi-power with self-learning; DIN 18032-3 certification=-; Descrizione=GWR5214B30K - ROAD5 MEDI WIDE 4M 3000K 1,0A CL2 BIREG; Device with reduced surface temperature=-; Driver=Included; Driver Box=Built-in; Efficiency (lm/W)=97; Electrocod=244C; Eletrical and lighting features=-; External screw=Stainless steel; Fixing=Pole Head - Outreach; Gasket=Anti-aging silicone; General information=-; Glow Wire Test :=-; IPEA=ROAD = B // LARGE AREAS = A ++ // CYCLOPEDONALS = B // GREEN AREAS = B // HISTORICAL CENTER = A3 +; Installationa and maintenance=-; LED Life Time (L80B05)=120000H; LED Maintenance=Not available; LED current.=1A; Lamp-=LED; Lifetime=L90B10 (Tq+25°C) = 100.000 h - L90B10 (Tq+40°C) = 50.000 h; Locking Hook=Integrated front handle; Lumen output (lm)=14800; Luminaire=LED Road Equipment; Materials=-; Maximum surface exposed to the wind=0,19M2; Maximum surface exposed to the wind :=0.19 m2; Minimum distance from the illuminated object=1M; Modello=GWR5214B30K; Mouting and installation=Pole Head - Outreach; Nominal flux (lm)=16560; Number of modules=4 (4x3 LED); Operating temperature :=-25 +40 °C; Operating temperature:=-25 +40 °C; Optic=WIDE; Optic :=Metallized polycarbonate reflector; Optic Maintenance=Not available; Optic and illuminating features=-; Overvoltage protection=DM 10KV / CM 10KV; Overvoltage resistance :=Common and dfferential mode: 10KV; Photobiological Risk Class=RG0; Power supply operation=Bi power; Rated frequency (Hz)=50 / 60; SEO=Street lighting; Shield type=4mm thick flat tempered glass; Standard Deviation Colour Matching=SDCM = 5; Standard-=EN 60598-2-3, EN 60598-1 IEC/TR 62778; Standards and approvals=-; Stocking temperature=-; Supply voltage=220 - 240 V; System power=153W; System power :=153 W @ 1A; Tilt adjustable=-20° ÷ +10° side bracket - -10° ÷ +20° pole head; Tilt-=-20° ÷ +10° side bracket - -10° ÷ +20° pole head; Tipo alimentatore=Constant Current Driver Led; Tipologia=Bi power; Type of light source=LED - Not replaceable; Unified Glare Rating=G*3 - ULOR = 0; Unique digital code (Datamatrix)=Currently not present; Voltage-=220/240 V - 50/60 Hz - Bi-power with self-learning; Weight (kg):=8,4; Wiring=Isolating switch
- GWR5256B - ROAD5 MEDI WIDE 6M 4000K 0,5A CL2 BIREG: Body=Die-cast aluminium -; Catalogue Range=ROAD [5]; Classification:=-; Color Rendering Index=CRI-70; Colore=Graphite grey; Colour :=Powder coating; Colour temperature=4000K; Colour temperature:=4000 K (CRI>70); Context=Street and parking lighting; Control System=Bi-power with self-learning; DIN 18032-3 certification=-; Descrizione=GWR5256B - ROAD5 MEDI WIDE 6M 4000K 0,5A CL2 BIREG; Device with reduced surface temperature=-; Driver=Included; Driver Box=Built-in; Efficiency (lm/W)=124; Electrocod=244C; Eletrical and lighting features=-; External screw=Stainless steel; Fixing=Pole Head - Outreach; Gasket=Anti-aging silicone; General information=-; Glow Wire Test :=-; IPEA=ROAD = A3 + // LARGE AREAS = A6 + // CYCLOPEDONALS = A3 + // GREEN AREAS = A3 + // HISTORICAL CENTER = A6 +; Installationa and maintenance=-; LED Life Time (L80B05)=120000H; LED Maintenance=Not available; LED current.=0,5A; Lamp-=LED; Lifetime=L90B10 (Tq+25°C) = 100.000 h - L90B10 (Tq+50°C) = 50.000 h; Locking Hook=Integrated front handle; Lumen output (lm)=14000; Luminaire=LED Road Equipment; Materials=-; Maximum surface exposed to the wind=0,19M2; Maximum surface exposed to the wind :=0.19 m2; Minimum distance from the illuminated object=1M; Modello=GWR5256B; Mouting and installation=Pole Head - Outreach; Nominal flux (lm)=14400; Number of modules=6 (6x3 LED); Operating temperature :=-25 +50 °C; Operating temperature:=-25 +40 °C; Optic=WIDE; Optic :=Metallized polycarbonate reflector; Optic Maintenance=Not available; Optic and illuminating features=-; Overvoltage protection=DM 10KV / CM 10KV; Photobiological Risk Class=RG0; Power supply operation=Bi power; Rated frequency (Hz)=50 / 60; SEO=Street lighting; Shield type=4mm thick flat tempered glass; Standard Deviation Colour Matching=SDCM = 5; Standard-=EN 60598-2-3, EN 60598-1 IEC/TR 62778; Standards and approvals=-; Stocking temperature=-; Supply voltage=220 - 240 V; System power=109W; System power :=113 W @ 0.5A; Tilt adjustable=-20° ÷ +10° side bracket - -10° ÷ +20° pole head; Tilt-=-20° ÷ +10° side bracket - -10° ÷ +20° pole head; Type of light source=LED - Not replaceable; Unified Glare Rating=G*3 - ULOR = 0; Unique digital code (Datamatrix)=Currently not present; Voltage-=220/240 V - 50/60 Hz - Bi-power with self-learning; Weight (kg):=9,09999999999999; Wiring=Isolating switch
- GWR5274V - ROAD5 MEDI V.WIDE 4M 4000K 0,7A CL2: Body=Die-cast aluminium -; Catalogue Range=ROAD [5]; Classification:=-; Color Rendering Index=CRI-70; Colore=Graphite grey; Colour :=Powder coating; Colour temperature=4000K; Colour temperature:=4000 K (CRI>70); Context=Street and parking lighting; Control System=DALI - 5 Step; DIN 18032-3 certification=-; Descrizione=GWR5274V - ROAD5 MEDI V.WIDE 4M 4000K 0,7A CL2; Device with reduced surface temperature=-; Driver=Included; Driver Box=Built-in; Efficiency (lm/W)=118; Electrocod=244C; Eletrical and lighting features=-; External screw=Stainless steel; Fixing=Pole Head - Outreach; Gasket=Anti-aging silicone; General information=-; Glow Wire Test :=-; IPEA=ROAD = A3 + // LARGE AREAS = A5 + // CYCLOPEDONALS = A ++ // GREEN AREAS = A ++ // HISTORICAL CENTER = A6 +; Installationa and maintenance=-; LED Life Time (L80B05)=120000H; LED Maintenance=Not available; LED current.=0,7A; Lamp-=LED; Lifetime=L90B10 (Tq+25°C) = 100.000 h - L90B10 (Tq+50°C) = 50.000 h; Locking Hook=Integrated front handle; Lumen output (lm)=12700; Luminaire=LED Road Equipment; Materials=-; Maximum surface exposed to the wind=0,19M2; Maximum surface exposed to the wind :=0.19 m2; Minimum distance from the illuminated object=1M; Modello=GWR5274V; Mouting and installation=Pole Head - Outreach; Nominal flux (lm)=12480; Number of modules=4 (4x3 LED); Operating temperature :=-25 +50 °C; Operating temperature:=-25 +40 °C; Optic=WIDE; Optic :=Metallized polycarbonate reflector; Optic Maintenance=Not available; Optic and illuminating features=-; Overvoltage protection=DM 10KV / CM 10KV; Photobiological Risk Class=RG0; Rated frequency (Hz)=50 / 60; SEO=Street lighting; Shield type=4mm thick flat tempered glass; Standard Deviation Colour Matching=SDCM = 5; Standard-=EN 60598-2-3, EN 60598-1 IEC/TR 62778; Standards and approvals=-; Stocking temperature=-; Supply voltage=220 - 240 V; System power=106W; System power :=108 W @ 0.7A; Tilt adjustable=-20° ÷ +10° side bracket - -10° ÷ +20° pole head; Tilt-=-20° ÷ +10° side bracket - -10° ÷ +20° pole head; Tipologia=Programmable (5 step); Type of light source=LED - Not replaceable; Unified Glare Rating=G*3 - ULOR = 0; Unique digital code (Datamatrix)=Currently not present; Voltage-=220/240 V - 50/60 Hz - Stand alone and/or programmable; Weight (kg):=8,4; Wiring=Isolating switch

## geometry (parser evidence)
native form markers: Blend x2
no freeform markers — native parametric forms only
